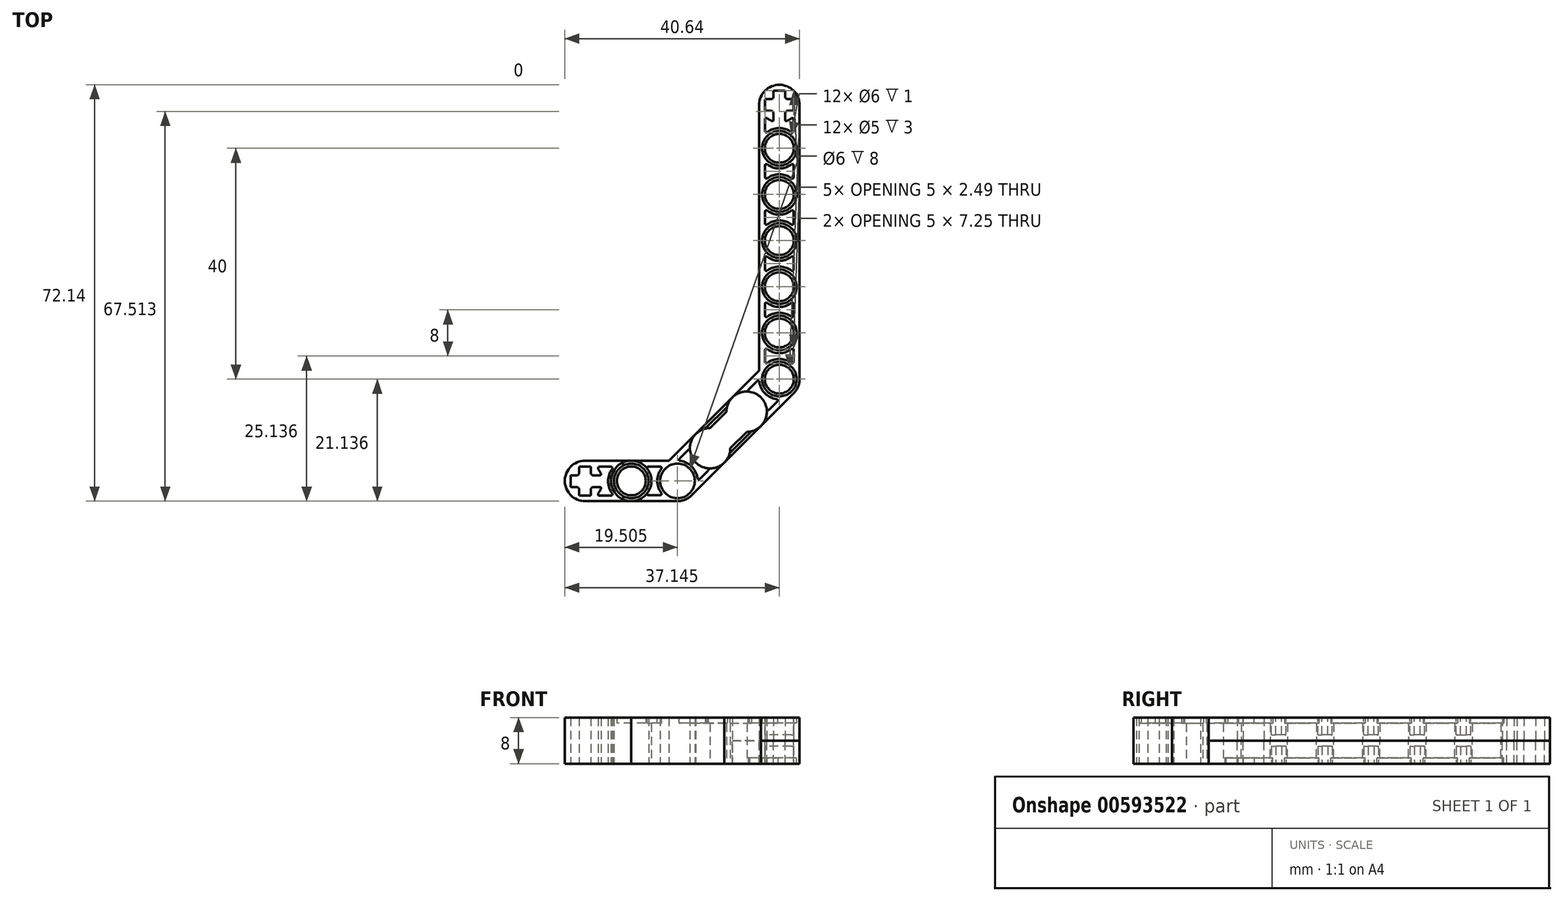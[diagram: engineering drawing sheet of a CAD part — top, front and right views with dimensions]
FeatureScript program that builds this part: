
annotation { "Feature Type Name" : "Feature", "Feature Type Description" : "" }
export const myFeature = defineFeature(function(context is Context, id is Id, definition is map)
    precondition{}
    {
        {
            var Q0;
            Q0=qCreatedBy(makeId("Top.planeOp"),FACE);
            var sketch = newSketch(context, id + "F0", { "sketchPlane" : qUnion([Q0])});
            skArc(sketch, "E0", {"start": v(42.78, 53.86) * mm, "mid": v(39.28, 57.36) * mm, "end": v(35.78, 53.86) * mm});
            skCircle(sketch, "E1", {"center": v(39.28, 6.36) * mm, "radius": 3.5 * mm});
            skLineSegment(sketch, "E2", {"start": v(35.78, 53.86) * mm, "end": v(35.78, 6.36) * mm});
            skLineSegment(sketch, "E3", {"start": v(42.78, 53.86) * mm, "end": v(42.78, 6.36) * mm});
            skCircle(sketch, "E4", {"center": v(39.28, 6.36) * mm, "radius": 2.5 * mm});
            skCircle(sketch, "E5", {"center": v(39.28, 6.36) * mm, "radius": 3 * mm});
            skCircle(sketch, "E6", {"center": v(21.64, -11.28) * mm, "radius": 3.5 * mm});
            skLineSegment(sketch, "E7", {"start": v(21.64, -11.28) * mm, "end": v(5.64, -11.28) * mm});
            skArc(sketch, "E8", {"start": v(5.64, -7.78) * mm, "mid": v(2.14, -11.28) * mm, "end": v(5.64, -14.78) * mm});
            skLineSegment(sketch, "E9", {"start": v(21.64, -7.78) * mm, "end": v(5.64, -7.78) * mm});
            skLineSegment(sketch, "E10", {"start": v(21.64, -14.78) * mm, "end": v(5.64, -14.78) * mm});
            skLineSegment(sketch, "E11", {"start": v(41.76, 3.88) * mm, "end": v(24.12, -13.76) * mm});
            skLineSegment(sketch, "E12", {"start": v(39.28, 6.36) * mm, "end": v(39.28, 14.36) * mm});
            skLineSegment(sketch, "E13", {"start": v(39.28, 14.36) * mm, "end": v(39.28, 22.36) * mm});
            skLineSegment(sketch, "E14", {"start": v(39.28, 22.36) * mm, "end": v(39.28, 30.36) * mm});
            skLineSegment(sketch, "E15", {"start": v(39.28, 30.36) * mm, "end": v(39.28, 38.36) * mm});
            skLineSegment(sketch, "E16", {"start": v(39.28, 38.36) * mm, "end": v(39.28, 46.36) * mm});
            skCircle(sketch, "E17", {"center": v(39.28, 14.36) * mm, "radius": 2.5 * mm});
            skCircle(sketch, "E18", {"center": v(39.28, 14.36) * mm, "radius": 3 * mm});
            skCircle(sketch, "E19", {"center": v(39.28, 14.36) * mm, "radius": 3.5 * mm});
            skCircle(sketch, "E20", {"center": v(39.28, 22.36) * mm, "radius": 2.5 * mm});
            skCircle(sketch, "E21", {"center": v(39.28, 22.36) * mm, "radius": 3 * mm});
            skCircle(sketch, "E22", {"center": v(39.28, 22.36) * mm, "radius": 3.5 * mm});
            skCircle(sketch, "E23", {"center": v(39.28, 30.36) * mm, "radius": 2.5 * mm});
            skCircle(sketch, "E24", {"center": v(39.28, 30.36) * mm, "radius": 3 * mm});
            skCircle(sketch, "E25", {"center": v(39.28, 30.36) * mm, "radius": 3.5 * mm});
            skCircle(sketch, "E26", {"center": v(39.28, 38.36) * mm, "radius": 2.5 * mm});
            skCircle(sketch, "E27", {"center": v(39.28, 38.36) * mm, "radius": 3 * mm});
            skCircle(sketch, "E28", {"center": v(39.28, 38.36) * mm, "radius": 3.5 * mm});
            skCircle(sketch, "E29", {"center": v(39.28, 46.36) * mm, "radius": 2.5 * mm});
            skCircle(sketch, "E30", {"center": v(39.28, 46.36) * mm, "radius": 3 * mm});
            skArc(sketch, "E31", {"start": v(35.78, 46.36) * mm, "mid": v(39.28, 42.86) * mm, "end": v(42.78, 46.36) * mm});
            skLineSegment(sketch, "E32", {"start": v(39.28, 56.36) * mm, "end": v(38.4, 56.36) * mm});
            skLineSegment(sketch, "E33", {"start": v(39.28, 56.36) * mm, "end": v(40.16, 56.36) * mm});
            skLineSegment(sketch, "E34", {"start": v(41.78, 53.86) * mm, "end": v(41.78, 54.74) * mm});
            skLineSegment(sketch, "E35", {"start": v(41.78, 53.86) * mm, "end": v(41.78, 52.98) * mm});
            skLineSegment(sketch, "E36", {"start": v(36.78, 53.86) * mm, "end": v(36.78, 54.74) * mm});
            skLineSegment(sketch, "E37", {"start": v(36.78, 53.86) * mm, "end": v(36.78, 52.98) * mm});
            skLineSegment(sketch, "E38", {"start": v(36.9, 54.86) * mm, "end": v(37.78, 54.86) * mm});
            skLineSegment(sketch, "E39", {"start": v(38.28, 55.36) * mm, "end": v(38.28, 56.24) * mm});
            skLineSegment(sketch, "E40", {"start": v(40.28, 56.24) * mm, "end": v(40.28, 55.36) * mm});
            skLineSegment(sketch, "E41", {"start": v(40.78, 54.86) * mm, "end": v(41.66, 54.86) * mm});
            skLineSegment(sketch, "E42", {"start": v(41.66, 52.86) * mm, "end": v(40.78, 52.86) * mm});
            skLineSegment(sketch, "E43", {"start": v(36.9, 52.86) * mm, "end": v(37.78, 52.86) * mm});
            skPoint(sketch, "E44.visualSharp", {"position": v(38.28, 56.36) * mm});
            skArc(sketch, "E44.filletArc", {"start": v(38.4, 56.36) * mm, "mid": v(38.32, 56.32) * mm, "end": v(38.28, 56.24) * mm});
            skPoint(sketch, "E45.visualSharp", {"position": v(40.28, 56.36) * mm});
            skArc(sketch, "E45.filletArc", {"start": v(40.28, 56.24) * mm, "mid": v(40.25, 56.32) * mm, "end": v(40.16, 56.36) * mm});
            skPoint(sketch, "E46.visualSharp", {"position": v(36.78, 54.86) * mm});
            skArc(sketch, "E46.filletArc", {"start": v(36.9, 54.86) * mm, "mid": v(36.82, 54.82) * mm, "end": v(36.78, 54.74) * mm});
            skPoint(sketch, "E47.visualSharp", {"position": v(36.78, 52.86) * mm});
            skArc(sketch, "E47.filletArc", {"start": v(36.78, 52.98) * mm, "mid": v(36.82, 52.9) * mm, "end": v(36.9, 52.86) * mm});
            skPoint(sketch, "E48.visualSharp", {"position": v(41.78, 54.86) * mm});
            skArc(sketch, "E48.filletArc", {"start": v(41.78, 54.74) * mm, "mid": v(41.75, 54.82) * mm, "end": v(41.66, 54.86) * mm});
            skPoint(sketch, "E49.visualSharp", {"position": v(41.78, 52.86) * mm});
            skArc(sketch, "E49.filletArc", {"start": v(41.66, 52.86) * mm, "mid": v(41.75, 52.9) * mm, "end": v(41.78, 52.98) * mm});
            skPoint(sketch, "E50.visualSharp", {"position": v(38.28, 54.86) * mm});
            skArc(sketch, "E50.filletArc", {"start": v(37.78, 54.86) * mm, "mid": v(38.14, 55) * mm, "end": v(38.28, 55.36) * mm});
            skPoint(sketch, "E51.visualSharp", {"position": v(40.28, 54.86) * mm});
            skArc(sketch, "E51.filletArc", {"start": v(40.28, 55.36) * mm, "mid": v(40.43, 55) * mm, "end": v(40.78, 54.86) * mm});
            skLineSegment(sketch, "E52", {"start": v(36.78, 50.1) * mm, "end": v(36.78, 49.36) * mm});
            skLineSegment(sketch, "E53", {"start": v(36.78, 50.1) * mm, "end": v(36.78, 51.35) * mm});
            skLineSegment(sketch, "E54", {"start": v(41.78, 50.04) * mm, "end": v(41.78, 49.36) * mm});
            skLineSegment(sketch, "E55", {"start": v(41.78, 50.04) * mm, "end": v(41.78, 51.35) * mm});
            skArc(sketch, "E56", {"start": v(37.19, 51.55) * mm, "mid": v(37.59, 51.3) * mm, "end": v(38.01, 51.1) * mm});
            skLineSegment(sketch, "E57.trimOffspring", {"start": v(39.28, 49.36) * mm, "end": v(39.28, 6.36) * mm});
            skLineSegment(sketch, "E58", {"start": v(40.28, 52.36) * mm, "end": v(40.28, 51.28) * mm});
            skLineSegment(sketch, "E59", {"start": v(38.28, 52.36) * mm, "end": v(38.28, 51.28) * mm});
            skPoint(sketch, "E60.visualSharp", {"position": v(38.28, 52.86) * mm});
            skArc(sketch, "E60.filletArc", {"start": v(38.28, 52.36) * mm, "mid": v(38.14, 52.7) * mm, "end": v(37.78, 52.86) * mm});
            skPoint(sketch, "E61.visualSharp", {"position": v(40.28, 52.86) * mm});
            skArc(sketch, "E61.filletArc", {"start": v(40.78, 52.86) * mm, "mid": v(40.43, 52.7) * mm, "end": v(40.28, 52.36) * mm});
            skArc(sketch, "E62.trimOffspring", {"start": v(40.56, 51.1) * mm, "mid": v(40.98, 51.3) * mm, "end": v(41.38, 51.55) * mm});
            skPoint(sketch, "E63.visualSharp", {"position": v(40.28, 51) * mm});
            skArc(sketch, "E63.filletArc", {"start": v(40.28, 51.28) * mm, "mid": v(40.37, 51.12) * mm, "end": v(40.56, 51.1) * mm});
            skPoint(sketch, "E64.visualSharp", {"position": v(38.28, 51) * mm});
            skArc(sketch, "E64.filletArc", {"start": v(38.01, 51.1) * mm, "mid": v(38.2, 51.12) * mm, "end": v(38.28, 51.28) * mm});
            skPoint(sketch, "E65.visualSharp", {"position": v(36.78, 51.9) * mm});
            skArc(sketch, "E65.filletArc", {"start": v(37.19, 51.55) * mm, "mid": v(36.92, 51.58) * mm, "end": v(36.78, 51.35) * mm});
            skArc(sketch, "E66.trimOffspring", {"start": v(41.38, 49.16) * mm, "mid": v(39.28, 49.86) * mm, "end": v(37.19, 49.16) * mm});
            skPoint(sketch, "E67.visualSharp", {"position": v(36.78, 48.8) * mm});
            skArc(sketch, "E67.filletArc", {"start": v(36.78, 49.36) * mm, "mid": v(36.92, 49.14) * mm, "end": v(37.19, 49.16) * mm});
            skPoint(sketch, "E68.visualSharp", {"position": v(41.78, 48.8) * mm});
            skArc(sketch, "E68.filletArc", {"start": v(41.38, 49.16) * mm, "mid": v(41.64, 49.14) * mm, "end": v(41.78, 49.36) * mm});
            skPoint(sketch, "E69.visualSharp", {"position": v(41.78, 51.9) * mm});
            skArc(sketch, "E69.filletArc", {"start": v(41.78, 51.35) * mm, "mid": v(41.64, 51.58) * mm, "end": v(41.38, 51.55) * mm});
            skLineSegment(sketch, "E70", {"start": v(3.13, -11.33) * mm, "end": v(3.13, -12.21) * mm});
            skLineSegment(sketch, "E71", {"start": v(3.13, -11.33) * mm, "end": v(3.13, -10.45) * mm});
            skLineSegment(sketch, "E72", {"start": v(5.63, -8.83) * mm, "end": v(4.75, -8.83) * mm});
            skLineSegment(sketch, "E73", {"start": v(5.63, -8.83) * mm, "end": v(6.51, -8.83) * mm});
            skLineSegment(sketch, "E74", {"start": v(5.63, -13.83) * mm, "end": v(4.75, -13.83) * mm});
            skLineSegment(sketch, "E75", {"start": v(5.63, -13.83) * mm, "end": v(6.51, -13.83) * mm});
            skLineSegment(sketch, "E76", {"start": v(4.63, -13.71) * mm, "end": v(4.63, -12.83) * mm});
            skLineSegment(sketch, "E77", {"start": v(4.13, -12.33) * mm, "end": v(3.25, -12.33) * mm});
            skLineSegment(sketch, "E78", {"start": v(3.25, -10.33) * mm, "end": v(4.13, -10.33) * mm});
            skLineSegment(sketch, "E79", {"start": v(4.63, -9.83) * mm, "end": v(4.63, -8.95) * mm});
            skLineSegment(sketch, "E80", {"start": v(6.63, -8.95) * mm, "end": v(6.63, -9.83) * mm});
            skLineSegment(sketch, "E81", {"start": v(6.63, -13.71) * mm, "end": v(6.63, -12.83) * mm});
            skPoint(sketch, "E82.visualSharp", {"position": v(3.13, -12.33) * mm});
            skArc(sketch, "E82.filletArc", {"start": v(3.13, -12.21) * mm, "mid": v(3.17, -12.3) * mm, "end": v(3.25, -12.33) * mm});
            skPoint(sketch, "E83.visualSharp", {"position": v(3.13, -10.33) * mm});
            skArc(sketch, "E83.filletArc", {"start": v(3.25, -10.33) * mm, "mid": v(3.17, -10.37) * mm, "end": v(3.13, -10.45) * mm});
            skPoint(sketch, "E84.visualSharp", {"position": v(4.63, -13.83) * mm});
            skArc(sketch, "E84.filletArc", {"start": v(4.63, -13.71) * mm, "mid": v(4.67, -13.8) * mm, "end": v(4.75, -13.83) * mm});
            skPoint(sketch, "E85.visualSharp", {"position": v(6.63, -13.83) * mm});
            skArc(sketch, "E85.filletArc", {"start": v(6.51, -13.83) * mm, "mid": v(6.6, -13.8) * mm, "end": v(6.63, -13.71) * mm});
            skPoint(sketch, "E86.visualSharp", {"position": v(4.63, -8.83) * mm});
            skArc(sketch, "E86.filletArc", {"start": v(4.75, -8.83) * mm, "mid": v(4.67, -8.87) * mm, "end": v(4.63, -8.95) * mm});
            skPoint(sketch, "E87.visualSharp", {"position": v(6.63, -8.83) * mm});
            skArc(sketch, "E87.filletArc", {"start": v(6.63, -8.95) * mm, "mid": v(6.6, -8.87) * mm, "end": v(6.51, -8.83) * mm});
            skPoint(sketch, "E88.visualSharp", {"position": v(4.63, -12.33) * mm});
            skArc(sketch, "E88.filletArc", {"start": v(4.63, -12.83) * mm, "mid": v(4.48, -12.48) * mm, "end": v(4.13, -12.33) * mm});
            skPoint(sketch, "E89.visualSharp", {"position": v(4.63, -10.33) * mm});
            skArc(sketch, "E89.filletArc", {"start": v(4.13, -10.33) * mm, "mid": v(4.48, -10.19) * mm, "end": v(4.63, -9.83) * mm});
            skLineSegment(sketch, "E90", {"start": v(9.39, -13.83) * mm, "end": v(10.13, -13.83) * mm});
            skLineSegment(sketch, "E91", {"start": v(9.39, -13.83) * mm, "end": v(8.14, -13.83) * mm});
            skLineSegment(sketch, "E92", {"start": v(9.45, -8.83) * mm, "end": v(10.13, -8.83) * mm});
            skLineSegment(sketch, "E93", {"start": v(9.45, -8.83) * mm, "end": v(8.14, -8.83) * mm});
            skArc(sketch, "E94", {"start": v(7.93, -13.43) * mm, "mid": v(8.2, -13.03) * mm, "end": v(8.4, -12.6) * mm});
            skLineSegment(sketch, "E95", {"start": v(7.13, -10.33) * mm, "end": v(8.2, -10.33) * mm});
            skLineSegment(sketch, "E96", {"start": v(7.13, -12.33) * mm, "end": v(8.2, -12.33) * mm});
            skPoint(sketch, "E97.visualSharp", {"position": v(6.63, -12.33) * mm});
            skArc(sketch, "E97.filletArc", {"start": v(7.13, -12.33) * mm, "mid": v(6.78, -12.48) * mm, "end": v(6.63, -12.83) * mm});
            skPoint(sketch, "E98.visualSharp", {"position": v(6.63, -10.33) * mm});
            skArc(sketch, "E98.filletArc", {"start": v(6.63, -9.83) * mm, "mid": v(6.78, -10.19) * mm, "end": v(7.13, -10.33) * mm});
            skArc(sketch, "E99.trimOffspring", {"start": v(8.4, -10.06) * mm, "mid": v(8.2, -9.63) * mm, "end": v(7.93, -9.24) * mm});
            skPoint(sketch, "E100.visualSharp", {"position": v(8.49, -10.33) * mm});
            skArc(sketch, "E100.filletArc", {"start": v(8.2, -10.33) * mm, "mid": v(8.37, -10.25) * mm, "end": v(8.4, -10.06) * mm});
            skPoint(sketch, "E101.visualSharp", {"position": v(8.49, -12.33) * mm});
            skArc(sketch, "E101.filletArc", {"start": v(8.4, -12.6) * mm, "mid": v(8.37, -12.42) * mm, "end": v(8.2, -12.33) * mm});
            skPoint(sketch, "E102.visualSharp", {"position": v(7.58, -13.83) * mm});
            skArc(sketch, "E102.filletArc", {"start": v(7.93, -13.43) * mm, "mid": v(7.91, -13.7) * mm, "end": v(8.14, -13.83) * mm});
            skArc(sketch, "E103.trimOffspring", {"start": v(10.33, -9.24) * mm, "mid": v(9.63, -11.33) * mm, "end": v(10.33, -13.43) * mm});
            skPoint(sketch, "E104.visualSharp", {"position": v(10.68, -13.83) * mm});
            skArc(sketch, "E104.filletArc", {"start": v(10.13, -13.83) * mm, "mid": v(10.35, -13.7) * mm, "end": v(10.33, -13.43) * mm});
            skPoint(sketch, "E105.visualSharp", {"position": v(10.68, -8.83) * mm});
            skArc(sketch, "E105.filletArc", {"start": v(10.33, -9.24) * mm, "mid": v(10.35, -8.97) * mm, "end": v(10.13, -8.83) * mm});
            skPoint(sketch, "E106.visualSharp", {"position": v(7.58, -8.83) * mm});
            skArc(sketch, "E106.filletArc", {"start": v(8.14, -8.83) * mm, "mid": v(7.91, -8.97) * mm, "end": v(7.93, -9.24) * mm});
            skLineSegment(sketch, "E107", {"start": v(21.64, -11.28) * mm, "end": v(39.28, 6.36) * mm});
            skLineSegment(sketch, "E108", {"start": v(21.64, -11.28) * mm, "end": v(13.64, -11.28) * mm});
            skCircle(sketch, "E109", {"center": v(13.64, -11.28) * mm, "radius": 3.5 * mm});
            skCircle(sketch, "E110", {"center": v(13.64, -11.28) * mm, "radius": 3 * mm});
            skCircle(sketch, "E111", {"center": v(13.64, -11.28) * mm, "radius": 2.5 * mm});
            skCircle(sketch, "E112", {"center": v(21.64, -11.28) * mm, "radius": 3 * mm});
            skCircle(sketch, "E113", {"center": v(21.64, -11.28) * mm, "radius": 2.5 * mm});
            skLineSegment(sketch, "E114", {"start": v(21.64, -11.28) * mm, "end": v(27.3, -5.63) * mm});
            skCircle(sketch, "E115", {"center": v(27.3, -5.63) * mm, "radius": 3.5 * mm});
            skLineSegment(sketch, "E116", {"start": v(39.28, 6.36) * mm, "end": v(33.63, 0.7) * mm});
            skCircle(sketch, "E117", {"center": v(33.63, 0.7) * mm, "radius": 3.5 * mm});
            skLineSegment(sketch, "E118", {"start": v(24.83, -3.15) * mm, "end": v(35.78, 7.8) * mm});
            skLineSegment(sketch, "E119", {"start": v(24.83, -3.15) * mm, "end": v(20.2, -7.78) * mm});
            skCircle(sketch, "E120", {"center": v(27.3, -5.63) * mm, "radius": 3 * mm});
            skCircle(sketch, "E121", {"center": v(27.3, -5.63) * mm, "radius": 2.5 * mm});
            skCircle(sketch, "E122", {"center": v(33.63, 0.7) * mm, "radius": 2.5 * mm});
            skLineSegment(sketch, "E123", {"start": v(31.86, 2.47) * mm, "end": v(25.53, -3.86) * mm});
            skLineSegment(sketch, "E124", {"start": v(29.07, -7.4) * mm, "end": v(35.4, -1.07) * mm});
            skSolve(sketch);
        }
        {
            var Q0;
            Q0=makeQuery(id+"F0.imprint","IMPRINT",FACE,{"disambiguationData":[TD([[makeQuery(id+"F0.imprint","IMPRINT",EDGE,{"derivedFrom":sQuery(id+"F0.wireOp",EDGE,"E70")}),-1.0]])]});
            var Q1;
            {var subQ0=sQuery(id+"F0.wireOp",EDGE,"E92");Q1=makeQuery(id+"F0.imprint","IMPRINT",FACE,{"disambiguationData":[TD([[makeQuery(id+"F0.imprint","IMPRINT",EDGE,{"derivedFrom":subQ0}),1.0]])]});}
            var Q2;
            Q2=makeQuery(id+"F0.imprint","IMPRINT",FACE,{"disambiguationData":[TD([[makeQuery(id+"F0.imprint","IMPRINT",EDGE,{"derivedFrom":sQuery(id+"F0.wireOp",EDGE,"E90")}),-1.0]])]});
            var Q3;
            {var subQ0=sQuery(id+"F0.wireOp",EDGE,"E10");var subQ1=sQuery(id+"F0.wireOp",EDGE,"E6");var subQ2=makeQuery(id+"F0.imprint","INTERSECT",VERTEX,{"derivedFrom":[subQ1,subQ0]});Q3=makeQuery(id+"F0.imprint","IMPRINT",FACE,{"disambiguationData":[TD([[makeQuery(id+"F0.imprint","IMPRINT",EDGE,{"disambiguationData":[TD([[subQ2,1.0]])],"derivedFrom":subQ1}),-1.0]])]});}
            var Q4;
            {var subQ1=sQuery(id+"F0.wireOp",EDGE,"E6");var subQ5=sQuery(id+"F0.wireOp",EDGE,"E9");var subQ6=makeQuery(id+"F0.imprint","INTERSECT",VERTEX,{"derivedFrom":[subQ1,subQ5]});Q4=makeQuery(id+"F0.imprint","IMPRINT",FACE,{"disambiguationData":[TD([[makeQuery(id+"F0.imprint","IMPRINT",EDGE,{"disambiguationData":[TD([[subQ6,-1.0]])],"derivedFrom":subQ1}),-1.0]])]});}
            var Q5;
            {var subQ2=sQuery(id+"F0.wireOp",EDGE,"E7");var subQ6=sQuery(id+"F0.wireOp",EDGE,"E110");var subQ7=makeQuery(id+"F0.imprint","INTERSECT",VERTEX,{"derivedFrom":[subQ2,subQ6]});Q5=makeQuery(id+"F0.imprint","IMPRINT",FACE,{"disambiguationData":[TD([[makeQuery(id+"F0.imprint","IMPRINT",EDGE,{"disambiguationData":[TD([[subQ7,-1.0]])],"derivedFrom":subQ2}),-1.0]])]});}
            var Q6;
            {var subQ4=sQuery(id+"F0.wireOp",EDGE,"E7");var subQ6=sQuery(id+"F0.wireOp",EDGE,"E110");var subQ8=makeQuery(id+"F0.imprint","INTERSECT",VERTEX,{"derivedFrom":[subQ4,subQ6]});Q6=makeQuery(id+"F0.imprint","IMPRINT",FACE,{"disambiguationData":[TD([[makeQuery(id+"F0.imprint","IMPRINT",EDGE,{"disambiguationData":[TD([[subQ8,-1.0]])],"derivedFrom":subQ4}),1.0]])]});}
            var Q7;
            {var subQ1=sQuery(id+"F0.wireOp",EDGE,"E6");var subQ7=makeQuery(id+"F0.imprint","INTERSECT",VERTEX,{"derivedFrom":[subQ1,sQuery(id+"F0.wireOp",EDGE,"E9")]});Q7=makeQuery(id+"F0.imprint","IMPRINT",FACE,{"disambiguationData":[TD([[makeQuery(id+"F0.imprint","IMPRINT",EDGE,{"disambiguationData":[TD([[subQ7,1.0]])],"derivedFrom":subQ1}),1.0]])]});}
            var Q8;
            {var subQ0=sQuery(id+"F0.wireOp",EDGE,"E119");Q8=makeQuery(id+"F0.imprint","IMPRINT",FACE,{"disambiguationData":[TD([[makeQuery(id+"F0.imprint","IMPRINT",EDGE,{"derivedFrom":subQ0}),1.0]])]});}
            var Q9;
            {var subQ0=sQuery(id+"F0.wireOp",EDGE,"E6");var subQ8=makeQuery(id+"F0.imprint","INTERSECT",VERTEX,{"derivedFrom":[subQ0,sQuery(id+"F0.wireOp",EDGE,"E10")]});Q9=makeQuery(id+"F0.imprint","IMPRINT",FACE,{"disambiguationData":[TD([[makeQuery(id+"F0.imprint","IMPRINT",EDGE,{"disambiguationData":[TD([[subQ8,1.0]])],"derivedFrom":subQ0}),1.0]])]});}
            var Q10;
            {var subQ0=sQuery(id+"F0.wireOp",EDGE,"E11");var subQ1=sQuery(id+"F0.wireOp",EDGE,"E6");var subQ2=makeQuery(id+"F0.imprint","INTERSECT",VERTEX,{"derivedFrom":[subQ1,subQ0]});Q10=makeQuery(id+"F0.imprint","IMPRINT",FACE,{"disambiguationData":[TD([[makeQuery(id+"F0.imprint","IMPRINT",EDGE,{"disambiguationData":[TD([[subQ2,-1.0]])],"derivedFrom":subQ1}),-1.0]])]});}
            var Q11;
            {var subQ0=sQuery(id+"F0.wireOp",EDGE,"E115");var subQ5=sQuery(id+"F0.wireOp",EDGE,"E114");var subQ8=makeQuery(id+"F0.imprint","INTERSECT",VERTEX,{"derivedFrom":[subQ5,subQ0]});Q11=makeQuery(id+"F0.imprint","IMPRINT",FACE,{"disambiguationData":[TD([[makeQuery(id+"F0.imprint","IMPRINT",EDGE,{"disambiguationData":[TD([[subQ8,-1.0]])],"derivedFrom":subQ5}),-1.0]])]});}
            var Q12;
            {var subQ0=sQuery(id+"F0.wireOp",EDGE,"E115");var subQ5=sQuery(id+"F0.wireOp",EDGE,"E114");var subQ8=makeQuery(id+"F0.imprint","INTERSECT",VERTEX,{"derivedFrom":[subQ5,subQ0]});Q12=makeQuery(id+"F0.imprint","IMPRINT",FACE,{"disambiguationData":[TD([[makeQuery(id+"F0.imprint","IMPRINT",EDGE,{"disambiguationData":[TD([[subQ8,-1.0]])],"derivedFrom":subQ5}),1.0]])]});}
            var Q13;
            {var subQ0=sQuery(id+"F0.wireOp",EDGE,"E118");var subQ5=sQuery(id+"F0.wireOp",EDGE,"E117");var subQ6=makeQuery(id+"F0.imprint","INTERSECT",VERTEX,{"derivedFrom":[subQ5,subQ0]});Q13=makeQuery(id+"F0.imprint","IMPRINT",FACE,{"disambiguationData":[TD([[makeQuery(id+"F0.imprint","IMPRINT",EDGE,{"disambiguationData":[TD([[subQ6,-1.0]])],"derivedFrom":subQ5}),-1.0]])]});}
            var Q14;
            {var subQ0=sQuery(id+"F0.wireOp",EDGE,"E120");var subQ1=sQuery(id+"F0.wireOp",EDGE,"E114");var subQ2=makeQuery(id+"F0.imprint","INTERSECT",VERTEX,{"derivedFrom":[subQ1,subQ0]});Q14=makeQuery(id+"F0.imprint","IMPRINT",FACE,{"disambiguationData":[TD([[makeQuery(id+"F0.imprint","IMPRINT",EDGE,{"disambiguationData":[TD([[subQ2,-1.0]])],"derivedFrom":subQ1}),1.0]])]});}
            var Q15;
            {var subQ0=sQuery(id+"F0.wireOp",EDGE,"E120");var subQ1=sQuery(id+"F0.wireOp",EDGE,"E114");var subQ2=makeQuery(id+"F0.imprint","INTERSECT",VERTEX,{"derivedFrom":[subQ1,subQ0]});Q15=makeQuery(id+"F0.imprint","IMPRINT",FACE,{"disambiguationData":[TD([[makeQuery(id+"F0.imprint","IMPRINT",EDGE,{"disambiguationData":[TD([[subQ2,-1.0]])],"derivedFrom":subQ1}),-1.0]])]});}
            var Q16;
            {var subQ0=sQuery(id+"F0.wireOp",EDGE,"E117");var subQ1=sQuery(id+"F0.wireOp",EDGE,"E11");var subQ2=makeQuery(id+"F0.imprint","INTERSECT",VERTEX,{"derivedFrom":[subQ1,subQ0]});Q16=makeQuery(id+"F0.imprint","IMPRINT",FACE,{"disambiguationData":[TD([[makeQuery(id+"F0.imprint","IMPRINT",EDGE,{"disambiguationData":[TD([[subQ2,-1.0]])],"derivedFrom":subQ1}),-1.0]])]});}
            var Q17;
            {var subQ3=sQuery(id+"F0.wireOp",EDGE,"E116");var subQ5=sQuery(id+"F0.wireOp",EDGE,"E117");var subQ6=makeQuery(id+"F0.imprint","INTERSECT",VERTEX,{"derivedFrom":[subQ3,subQ5]});Q17=makeQuery(id+"F0.imprint","IMPRINT",FACE,{"disambiguationData":[TD([[makeQuery(id+"F0.imprint","IMPRINT",EDGE,{"disambiguationData":[TD([[subQ6,-1.0]])],"derivedFrom":subQ3}),1.0]])]});}
            var Q18;
            {var subQ3=sQuery(id+"F0.wireOp",EDGE,"E116");var subQ5=sQuery(id+"F0.wireOp",EDGE,"E117");var subQ8=makeQuery(id+"F0.imprint","INTERSECT",VERTEX,{"derivedFrom":[subQ3,subQ5]});Q18=makeQuery(id+"F0.imprint","IMPRINT",FACE,{"disambiguationData":[TD([[makeQuery(id+"F0.imprint","IMPRINT",EDGE,{"disambiguationData":[TD([[subQ8,-1.0]])],"derivedFrom":subQ3}),-1.0]])]});}
            var Q19;
            {var subQ0=sQuery(id+"F0.wireOp",EDGE,"E11");var subQ1=sQuery(id+"F0.wireOp",EDGE,"E1");var subQ2=makeQuery(id+"F0.imprint","INTERSECT",VERTEX,{"derivedFrom":[subQ1,subQ0]});Q19=makeQuery(id+"F0.imprint","IMPRINT",FACE,{"disambiguationData":[TD([[makeQuery(id+"F0.imprint","IMPRINT",EDGE,{"disambiguationData":[TD([[subQ2,1.0]])],"derivedFrom":subQ1}),-1.0]])]});}
            var Q20;
            {var subQ1=sQuery(id+"F0.wireOp",EDGE,"E1");var subQ5=sQuery(id+"F0.wireOp",EDGE,"E2");var subQ6=makeQuery(id+"F0.imprint","INTERSECT",VERTEX,{"derivedFrom":[subQ1,subQ5]});Q20=makeQuery(id+"F0.imprint","IMPRINT",FACE,{"disambiguationData":[TD([[makeQuery(id+"F0.imprint","IMPRINT",EDGE,{"disambiguationData":[TD([[subQ6,-1.0]])],"derivedFrom":subQ1}),-1.0]])]});}
            var Q21;
            {var subQ5=sQuery(id+"F0.wireOp",EDGE,"E1");var subQ6=makeQuery(id+"F0.imprint","INTERSECT",VERTEX,{"derivedFrom":[subQ5,sQuery(id+"F0.wireOp",EDGE,"E3")]});Q21=makeQuery(id+"F0.imprint","IMPRINT",FACE,{"disambiguationData":[TD([[makeQuery(id+"F0.imprint","IMPRINT",EDGE,{"disambiguationData":[TD([[subQ6,-1.0]])],"derivedFrom":subQ5}),1.0]])]});}
            var Q22;
            {var subQ0=sQuery(id+"F0.wireOp",EDGE,"E3");var subQ1=sQuery(id+"F0.wireOp",EDGE,"E1");var subQ2=makeQuery(id+"F0.imprint","INTERSECT",VERTEX,{"derivedFrom":[subQ1,subQ0]});Q22=makeQuery(id+"F0.imprint","IMPRINT",FACE,{"disambiguationData":[TD([[makeQuery(id+"F0.imprint","IMPRINT",EDGE,{"disambiguationData":[TD([[subQ2,-1.0]])],"derivedFrom":subQ1}),-1.0]])]});}
            var Q23;
            {var subQ0=sQuery(id+"F0.wireOp",EDGE,"E2");var subQ6=sQuery(id+"F0.wireOp",EDGE,"E1");var subQ7=makeQuery(id+"F0.imprint","INTERSECT",VERTEX,{"derivedFrom":[subQ6,subQ0]});Q23=makeQuery(id+"F0.imprint","IMPRINT",FACE,{"disambiguationData":[TD([[makeQuery(id+"F0.imprint","IMPRINT",EDGE,{"disambiguationData":[TD([[subQ7,1.0]])],"derivedFrom":subQ6}),-1.0]])]});}
            var Q24;
            {var subQ5=sQuery(id+"F0.wireOp",EDGE,"E1");var subQ7=makeQuery(id+"F0.imprint","INTERSECT",VERTEX,{"derivedFrom":[subQ5,sQuery(id+"F0.wireOp",EDGE,"E2")]});Q24=makeQuery(id+"F0.imprint","IMPRINT",FACE,{"disambiguationData":[TD([[makeQuery(id+"F0.imprint","IMPRINT",EDGE,{"disambiguationData":[TD([[subQ7,1.0]])],"derivedFrom":subQ5}),1.0]])]});}
            var Q25;
            {var subQ0=sQuery(id+"F0.wireOp",EDGE,"E57.trimOffspring");var subQ1=sQuery(id+"F0.wireOp",EDGE,"E18");var subQ2=makeQuery(id+"F0.imprint","INTERSECT",VERTEX,{"disambiguationData":[OD(0.0)],"derivedFrom":[subQ1,subQ0]});Q25=makeQuery(id+"F0.imprint","IMPRINT",FACE,{"disambiguationData":[TD([[makeQuery(id+"F0.imprint","IMPRINT",EDGE,{"disambiguationData":[TD([[subQ2,1.0]])],"derivedFrom":subQ1}),-1.0]])]});}
            var Q26;
            {var subQ0=sQuery(id+"F0.wireOp",EDGE,"E57.trimOffspring");var subQ1=sQuery(id+"F0.wireOp",EDGE,"E18");var subQ2=makeQuery(id+"F0.imprint","INTERSECT",VERTEX,{"disambiguationData":[OD(0.0)],"derivedFrom":[subQ1,subQ0]});Q26=makeQuery(id+"F0.imprint","IMPRINT",FACE,{"disambiguationData":[TD([[makeQuery(id+"F0.imprint","IMPRINT",EDGE,{"disambiguationData":[TD([[subQ2,-1.0]])],"derivedFrom":subQ1}),-1.0]])]});}
            var Q27;
            {var subQ0=sQuery(id+"F0.wireOp",EDGE,"E22");var subQ1=sQuery(id+"F0.wireOp",EDGE,"E3");var subQ2=makeQuery(id+"F0.imprint","INTERSECT",VERTEX,{"derivedFrom":[subQ1,subQ0]});Q27=makeQuery(id+"F0.imprint","IMPRINT",FACE,{"disambiguationData":[TD([[makeQuery(id+"F0.imprint","IMPRINT",EDGE,{"disambiguationData":[TD([[subQ2,-1.0]])],"derivedFrom":subQ1}),-1.0]])]});}
            var Q28;
            {var subQ0=sQuery(id+"F0.wireOp",EDGE,"E22");var subQ1=sQuery(id+"F0.wireOp",EDGE,"E2");var subQ2=makeQuery(id+"F0.imprint","INTERSECT",VERTEX,{"derivedFrom":[subQ1,subQ0]});Q28=makeQuery(id+"F0.imprint","IMPRINT",FACE,{"disambiguationData":[TD([[makeQuery(id+"F0.imprint","IMPRINT",EDGE,{"disambiguationData":[TD([[subQ2,-1.0]])],"derivedFrom":subQ1}),1.0]])]});}
            var Q29;
            {var subQ0=sQuery(id+"F0.wireOp",EDGE,"E57.trimOffspring");var subQ1=sQuery(id+"F0.wireOp",EDGE,"E21");var subQ2=makeQuery(id+"F0.imprint","INTERSECT",VERTEX,{"disambiguationData":[OD(0.0)],"derivedFrom":[subQ1,subQ0]});Q29=makeQuery(id+"F0.imprint","IMPRINT",FACE,{"disambiguationData":[TD([[makeQuery(id+"F0.imprint","IMPRINT",EDGE,{"disambiguationData":[TD([[subQ2,1.0]])],"derivedFrom":subQ1}),-1.0]])]});}
            var Q30;
            {var subQ0=sQuery(id+"F0.wireOp",EDGE,"E25");var subQ1=sQuery(id+"F0.wireOp",EDGE,"E3");var subQ2=makeQuery(id+"F0.imprint","INTERSECT",VERTEX,{"derivedFrom":[subQ1,subQ0]});Q30=makeQuery(id+"F0.imprint","IMPRINT",FACE,{"disambiguationData":[TD([[makeQuery(id+"F0.imprint","IMPRINT",EDGE,{"disambiguationData":[TD([[subQ2,-1.0]])],"derivedFrom":subQ1}),-1.0]])]});}
            var Q31;
            {var subQ0=sQuery(id+"F0.wireOp",EDGE,"E25");var subQ1=sQuery(id+"F0.wireOp",EDGE,"E2");var subQ2=makeQuery(id+"F0.imprint","INTERSECT",VERTEX,{"derivedFrom":[subQ1,subQ0]});Q31=makeQuery(id+"F0.imprint","IMPRINT",FACE,{"disambiguationData":[TD([[makeQuery(id+"F0.imprint","IMPRINT",EDGE,{"disambiguationData":[TD([[subQ2,-1.0]])],"derivedFrom":subQ1}),1.0]])]});}
            var Q32;
            {var subQ2=sQuery(id+"F0.wireOp",EDGE,"E57.trimOffspring");var subQ4=sQuery(id+"F0.wireOp",EDGE,"E21");var subQ5=makeQuery(id+"F0.imprint","INTERSECT",VERTEX,{"disambiguationData":[OD(0.0)],"derivedFrom":[subQ4,subQ2]});Q32=makeQuery(id+"F0.imprint","IMPRINT",FACE,{"disambiguationData":[TD([[makeQuery(id+"F0.imprint","IMPRINT",EDGE,{"disambiguationData":[TD([[subQ5,-1.0]])],"derivedFrom":subQ4}),-1.0]])]});}
            var Q33;
            {var subQ2=sQuery(id+"F0.wireOp",EDGE,"E57.trimOffspring");var subQ4=sQuery(id+"F0.wireOp",EDGE,"E24");var subQ7=makeQuery(id+"F0.imprint","INTERSECT",VERTEX,{"disambiguationData":[OD(0.0)],"derivedFrom":[subQ4,subQ2]});Q33=makeQuery(id+"F0.imprint","IMPRINT",FACE,{"disambiguationData":[TD([[makeQuery(id+"F0.imprint","IMPRINT",EDGE,{"disambiguationData":[TD([[subQ7,1.0]])],"derivedFrom":subQ4}),-1.0]])]});}
            var Q34;
            {var subQ0=sQuery(id+"F0.wireOp",EDGE,"E28");var subQ1=sQuery(id+"F0.wireOp",EDGE,"E3");var subQ2=makeQuery(id+"F0.imprint","INTERSECT",VERTEX,{"derivedFrom":[subQ1,subQ0]});Q34=makeQuery(id+"F0.imprint","IMPRINT",FACE,{"disambiguationData":[TD([[makeQuery(id+"F0.imprint","IMPRINT",EDGE,{"disambiguationData":[TD([[subQ2,-1.0]])],"derivedFrom":subQ1}),-1.0]])]});}
            var Q35;
            {var subQ0=sQuery(id+"F0.wireOp",EDGE,"E28");var subQ1=sQuery(id+"F0.wireOp",EDGE,"E2");var subQ2=makeQuery(id+"F0.imprint","INTERSECT",VERTEX,{"derivedFrom":[subQ1,subQ0]});Q35=makeQuery(id+"F0.imprint","IMPRINT",FACE,{"disambiguationData":[TD([[makeQuery(id+"F0.imprint","IMPRINT",EDGE,{"disambiguationData":[TD([[subQ2,-1.0]])],"derivedFrom":subQ1}),1.0]])]});}
            var Q36;
            {var subQ0=sQuery(id+"F0.wireOp",EDGE,"E57.trimOffspring");var subQ1=sQuery(id+"F0.wireOp",EDGE,"E24");var subQ2=makeQuery(id+"F0.imprint","INTERSECT",VERTEX,{"disambiguationData":[OD(0.0)],"derivedFrom":[subQ1,subQ0]});Q36=makeQuery(id+"F0.imprint","IMPRINT",FACE,{"disambiguationData":[TD([[makeQuery(id+"F0.imprint","IMPRINT",EDGE,{"disambiguationData":[TD([[subQ2,-1.0]])],"derivedFrom":subQ1}),-1.0]])]});}
            var Q37;
            {var subQ0=sQuery(id+"F0.wireOp",EDGE,"E57.trimOffspring");var subQ1=sQuery(id+"F0.wireOp",EDGE,"E27");var subQ2=makeQuery(id+"F0.imprint","INTERSECT",VERTEX,{"disambiguationData":[OD(0.0)],"derivedFrom":[subQ1,subQ0]});Q37=makeQuery(id+"F0.imprint","IMPRINT",FACE,{"disambiguationData":[TD([[makeQuery(id+"F0.imprint","IMPRINT",EDGE,{"disambiguationData":[TD([[subQ2,-1.0]])],"derivedFrom":subQ1}),-1.0]])]});}
            var Q38;
            {var subQ2=sQuery(id+"F0.wireOp",EDGE,"E57.trimOffspring");var subQ4=sQuery(id+"F0.wireOp",EDGE,"E27");var subQ5=makeQuery(id+"F0.imprint","INTERSECT",VERTEX,{"disambiguationData":[OD(0.0)],"derivedFrom":[subQ4,subQ2]});Q38=makeQuery(id+"F0.imprint","IMPRINT",FACE,{"disambiguationData":[TD([[makeQuery(id+"F0.imprint","IMPRINT",EDGE,{"disambiguationData":[TD([[subQ5,1.0]])],"derivedFrom":subQ4}),-1.0]])]});}
            var Q39;
            {var subQ0=sQuery(id+"F0.wireOp",EDGE,"E31");var subQ1=sQuery(id+"F0.wireOp",EDGE,"E3");var subQ2=makeQuery(id+"F0.imprint","INTERSECT",VERTEX,{"derivedFrom":[subQ1,subQ0]});Q39=makeQuery(id+"F0.imprint","IMPRINT",FACE,{"disambiguationData":[TD([[makeQuery(id+"F0.imprint","IMPRINT",EDGE,{"disambiguationData":[TD([[subQ2,-1.0]])],"derivedFrom":subQ1}),-1.0]])]});}
            var Q40;
            {var subQ0=sQuery(id+"F0.wireOp",EDGE,"E31");var subQ1=sQuery(id+"F0.wireOp",EDGE,"E2");var subQ2=makeQuery(id+"F0.imprint","INTERSECT",VERTEX,{"derivedFrom":[subQ1,subQ0]});Q40=makeQuery(id+"F0.imprint","IMPRINT",FACE,{"disambiguationData":[TD([[makeQuery(id+"F0.imprint","IMPRINT",EDGE,{"disambiguationData":[TD([[subQ2,-1.0]])],"derivedFrom":subQ1}),1.0]])]});}
            var Q41;
            {var subQ0=sQuery(id+"F0.wireOp",EDGE,"E0");Q41=makeQuery(id+"F0.imprint","IMPRINT",FACE,{"disambiguationData":[TD([[makeQuery(id+"F0.imprint","IMPRINT",EDGE,{"derivedFrom":subQ0}),1.0]])]});}
            extrude(context, id + "F1", {"entities" : qUnion([Q0, Q1, Q2, Q3, Q4, Q5, Q6, Q7, Q8, Q9, Q10, Q11, Q12, Q13, Q14, Q15, Q16, Q17, Q18, Q19, Q20, Q21, Q22, Q23, Q24, Q25, Q26, Q27, Q28, Q29, Q30, Q31, Q32, Q33, Q34, Q35, Q36, Q37, Q38, Q39, Q40, Q41]), "depth" : 8 * mm, "offsetDistance" : 25 * mm});
        }
        {
            var Q0;
            Q0=makeQuery(id+"F1.opExtrude","CAP_FACE",FACE,{"disambiguationData":[OSD([sQuery(id+"F0.wireOp",EDGE,"E0"),sQuery(id+"F0.wireOp",EDGE,"E1"),sQuery(id+"F0.wireOp",EDGE,"E2"),sQuery(id+"F0.wireOp",EDGE,"E3"),sQuery(id+"F0.wireOp",EDGE,"E5"),sQuery(id+"F0.wireOp",EDGE,"E6"),sQuery(id+"F0.wireOp",EDGE,"E8"),sQuery(id+"F0.wireOp",EDGE,"E9"),sQuery(id+"F0.wireOp",EDGE,"E10"),sQuery(id+"F0.wireOp",EDGE,"E11"),sQuery(id+"F0.wireOp",EDGE,"E18"),sQuery(id+"F0.wireOp",EDGE,"E21"),sQuery(id+"F0.wireOp",EDGE,"E24"),sQuery(id+"F0.wireOp",EDGE,"E27"),sQuery(id+"F0.wireOp",EDGE,"E30"),sQuery(id+"F0.wireOp",EDGE,"E32"),sQuery(id+"F0.wireOp",EDGE,"E33"),sQuery(id+"F0.wireOp",EDGE,"E34"),sQuery(id+"F0.wireOp",EDGE,"E35"),sQuery(id+"F0.wireOp",EDGE,"E36"),sQuery(id+"F0.wireOp",EDGE,"E37"),sQuery(id+"F0.wireOp",EDGE,"E38"),sQuery(id+"F0.wireOp",EDGE,"E39"),sQuery(id+"F0.wireOp",EDGE,"E40"),sQuery(id+"F0.wireOp",EDGE,"E41"),sQuery(id+"F0.wireOp",EDGE,"E42"),sQuery(id+"F0.wireOp",EDGE,"E43"),sQuery(id+"F0.wireOp",EDGE,"E44.filletArc"),sQuery(id+"F0.wireOp",EDGE,"E45.filletArc"),sQuery(id+"F0.wireOp",EDGE,"E46.filletArc"),sQuery(id+"F0.wireOp",EDGE,"E47.filletArc"),sQuery(id+"F0.wireOp",EDGE,"E48.filletArc"),sQuery(id+"F0.wireOp",EDGE,"E49.filletArc"),sQuery(id+"F0.wireOp",EDGE,"E50.filletArc"),sQuery(id+"F0.wireOp",EDGE,"E51.filletArc"),sQuery(id+"F0.wireOp",EDGE,"E52"),sQuery(id+"F0.wireOp",EDGE,"E53"),sQuery(id+"F0.wireOp",EDGE,"E54"),sQuery(id+"F0.wireOp",EDGE,"E55"),sQuery(id+"F0.wireOp",EDGE,"E56"),sQuery(id+"F0.wireOp",EDGE,"E58"),sQuery(id+"F0.wireOp",EDGE,"E59"),sQuery(id+"F0.wireOp",EDGE,"E60.filletArc"),sQuery(id+"F0.wireOp",EDGE,"E61.filletArc"),sQuery(id+"F0.wireOp",EDGE,"E62.trimOffspring"),sQuery(id+"F0.wireOp",EDGE,"E63.filletArc"),sQuery(id+"F0.wireOp",EDGE,"E64.filletArc"),sQuery(id+"F0.wireOp",EDGE,"E65.filletArc"),sQuery(id+"F0.wireOp",EDGE,"E66.trimOffspring"),sQuery(id+"F0.wireOp",EDGE,"E67.filletArc"),sQuery(id+"F0.wireOp",EDGE,"E68.filletArc"),sQuery(id+"F0.wireOp",EDGE,"E69.filletArc"),sQuery(id+"F0.wireOp",EDGE,"E70"),sQuery(id+"F0.wireOp",EDGE,"E71"),sQuery(id+"F0.wireOp",EDGE,"E72"),sQuery(id+"F0.wireOp",EDGE,"E73"),sQuery(id+"F0.wireOp",EDGE,"E74"),sQuery(id+"F0.wireOp",EDGE,"E75"),sQuery(id+"F0.wireOp",EDGE,"E76"),sQuery(id+"F0.wireOp",EDGE,"E77"),sQuery(id+"F0.wireOp",EDGE,"E78"),sQuery(id+"F0.wireOp",EDGE,"E79"),sQuery(id+"F0.wireOp",EDGE,"E80"),sQuery(id+"F0.wireOp",EDGE,"E81"),sQuery(id+"F0.wireOp",EDGE,"E82.filletArc"),sQuery(id+"F0.wireOp",EDGE,"E83.filletArc"),sQuery(id+"F0.wireOp",EDGE,"E84.filletArc"),sQuery(id+"F0.wireOp",EDGE,"E85.filletArc"),sQuery(id+"F0.wireOp",EDGE,"E86.filletArc"),sQuery(id+"F0.wireOp",EDGE,"E87.filletArc"),sQuery(id+"F0.wireOp",EDGE,"E88.filletArc"),sQuery(id+"F0.wireOp",EDGE,"E89.filletArc"),sQuery(id+"F0.wireOp",EDGE,"E90"),sQuery(id+"F0.wireOp",EDGE,"E91"),sQuery(id+"F0.wireOp",EDGE,"E92"),sQuery(id+"F0.wireOp",EDGE,"E93"),sQuery(id+"F0.wireOp",EDGE,"E94"),sQuery(id+"F0.wireOp",EDGE,"E95"),sQuery(id+"F0.wireOp",EDGE,"E96"),sQuery(id+"F0.wireOp",EDGE,"E97.filletArc"),sQuery(id+"F0.wireOp",EDGE,"E98.filletArc"),sQuery(id+"F0.wireOp",EDGE,"E99.trimOffspring"),sQuery(id+"F0.wireOp",EDGE,"E100.filletArc"),sQuery(id+"F0.wireOp",EDGE,"E101.filletArc"),sQuery(id+"F0.wireOp",EDGE,"E102.filletArc"),sQuery(id+"F0.wireOp",EDGE,"E103.trimOffspring"),sQuery(id+"F0.wireOp",EDGE,"E104.filletArc"),sQuery(id+"F0.wireOp",EDGE,"E105.filletArc"),sQuery(id+"F0.wireOp",EDGE,"E106.filletArc"),sQuery(id+"F0.wireOp",EDGE,"E110"),sQuery(id+"F0.wireOp",EDGE,"E112"),sQuery(id+"F0.wireOp",EDGE,"E118"),sQuery(id+"F0.wireOp",EDGE,"E119"),sQuery(id+"F0.wireOp",EDGE,"E121"),sQuery(id+"F0.wireOp",EDGE,"E122"),sQuery(id+"F0.wireOp",EDGE,"E123"),sQuery(id+"F0.wireOp",EDGE,"E124")])],"isStart":false});
            var sketch = newSketch(context, id + "F2", { "sketchPlane" : qUnion([Q0])});
            skArc(sketch, "E125", {"start": v(37.19, 43.55) * mm, "mid": v(39.28, 42.86) * mm, "end": v(41.38, 43.55) * mm});
            skArc(sketch, "E126", {"start": v(41.38, 41.16) * mm, "mid": v(39.28, 41.86) * mm, "end": v(37.19, 41.16) * mm});
            skLineSegment(sketch, "E127", {"start": v(36.78, 42.33) * mm, "end": v(36.78, 41.36) * mm});
            skLineSegment(sketch, "E128", {"start": v(36.78, 42.33) * mm, "end": v(36.78, 43.35) * mm});
            skLineSegment(sketch, "E129", {"start": v(41.78, 42.42) * mm, "end": v(41.78, 41.36) * mm});
            skLineSegment(sketch, "E130", {"start": v(41.78, 42.42) * mm, "end": v(41.78, 43.35) * mm});
            skPoint(sketch, "E131.visualSharp", {"position": v(36.78, 40.8) * mm});
            skArc(sketch, "E131.filletArc", {"start": v(36.78, 41.36) * mm, "mid": v(36.92, 41.14) * mm, "end": v(37.19, 41.16) * mm});
            skPoint(sketch, "E132.visualSharp", {"position": v(36.78, 43.9) * mm});
            skArc(sketch, "E132.filletArc", {"start": v(37.19, 43.55) * mm, "mid": v(36.92, 43.58) * mm, "end": v(36.78, 43.35) * mm});
            skPoint(sketch, "E133.visualSharp", {"position": v(41.78, 43.9) * mm});
            skArc(sketch, "E133.filletArc", {"start": v(41.78, 43.35) * mm, "mid": v(41.64, 43.58) * mm, "end": v(41.38, 43.55) * mm});
            skPoint(sketch, "E134.visualSharp", {"position": v(41.78, 40.8) * mm});
            skArc(sketch, "E134.filletArc", {"start": v(41.38, 41.16) * mm, "mid": v(41.64, 41.14) * mm, "end": v(41.78, 41.36) * mm});
            skArc(sketch, "E135.0.1.0", {"start": v(41.38, 33.16) * mm, "mid": v(39.28, 33.86) * mm, "end": v(37.19, 33.16) * mm});
            skLineSegment(sketch, "E135.0.1.1", {"start": v(36.78, 34.33) * mm, "end": v(36.78, 33.36) * mm});
            skArc(sketch, "E135.0.1.2", {"start": v(36.78, 33.36) * mm, "mid": v(36.92, 33.14) * mm, "end": v(37.19, 33.16) * mm});
            skLineSegment(sketch, "E135.0.1.3", {"start": v(36.78, 34.33) * mm, "end": v(36.78, 35.35) * mm});
            skArc(sketch, "E135.0.1.4", {"start": v(37.19, 35.55) * mm, "mid": v(36.92, 35.58) * mm, "end": v(36.78, 35.35) * mm});
            skArc(sketch, "E135.0.1.5", {"start": v(37.19, 35.55) * mm, "mid": v(39.28, 34.86) * mm, "end": v(41.38, 35.55) * mm});
            skLineSegment(sketch, "E135.0.1.6", {"start": v(41.78, 34.42) * mm, "end": v(41.78, 33.36) * mm});
            skArc(sketch, "E135.0.1.7", {"start": v(41.38, 33.16) * mm, "mid": v(41.64, 33.14) * mm, "end": v(41.78, 33.36) * mm});
            skLineSegment(sketch, "E135.0.1.8", {"start": v(41.78, 34.42) * mm, "end": v(41.78, 35.35) * mm});
            skArc(sketch, "E135.0.1.9", {"start": v(41.78, 35.35) * mm, "mid": v(41.64, 35.58) * mm, "end": v(41.38, 35.55) * mm});
            skArc(sketch, "E135.0.2.0", {"start": v(41.38, 25.16) * mm, "mid": v(39.28, 25.86) * mm, "end": v(37.19, 25.16) * mm});
            skLineSegment(sketch, "E135.0.2.1", {"start": v(36.78, 26.33) * mm, "end": v(36.78, 25.36) * mm});
            skArc(sketch, "E135.0.2.2", {"start": v(36.78, 25.36) * mm, "mid": v(36.92, 25.14) * mm, "end": v(37.19, 25.16) * mm});
            skLineSegment(sketch, "E135.0.2.3", {"start": v(36.78, 26.33) * mm, "end": v(36.78, 27.35) * mm});
            skArc(sketch, "E135.0.2.4", {"start": v(37.19, 27.55) * mm, "mid": v(36.92, 27.58) * mm, "end": v(36.78, 27.35) * mm});
            skArc(sketch, "E135.0.2.5", {"start": v(37.19, 27.55) * mm, "mid": v(39.28, 26.86) * mm, "end": v(41.38, 27.55) * mm});
            skLineSegment(sketch, "E135.0.2.6", {"start": v(41.78, 26.42) * mm, "end": v(41.78, 25.36) * mm});
            skArc(sketch, "E135.0.2.7", {"start": v(41.38, 25.16) * mm, "mid": v(41.64, 25.14) * mm, "end": v(41.78, 25.36) * mm});
            skLineSegment(sketch, "E135.0.2.8", {"start": v(41.78, 26.42) * mm, "end": v(41.78, 27.35) * mm});
            skArc(sketch, "E135.0.2.9", {"start": v(41.78, 27.35) * mm, "mid": v(41.64, 27.58) * mm, "end": v(41.38, 27.55) * mm});
            skArc(sketch, "E135.0.3.0", {"start": v(41.38, 17.16) * mm, "mid": v(39.28, 17.86) * mm, "end": v(37.19, 17.16) * mm});
            skLineSegment(sketch, "E135.0.3.1", {"start": v(36.78, 18.33) * mm, "end": v(36.78, 17.36) * mm});
            skArc(sketch, "E135.0.3.2", {"start": v(36.78, 17.36) * mm, "mid": v(36.92, 17.14) * mm, "end": v(37.19, 17.16) * mm});
            skLineSegment(sketch, "E135.0.3.3", {"start": v(36.78, 18.33) * mm, "end": v(36.78, 19.35) * mm});
            skArc(sketch, "E135.0.3.4", {"start": v(37.19, 19.55) * mm, "mid": v(36.92, 19.58) * mm, "end": v(36.78, 19.35) * mm});
            skArc(sketch, "E135.0.3.5", {"start": v(37.19, 19.55) * mm, "mid": v(39.28, 18.86) * mm, "end": v(41.38, 19.55) * mm});
            skLineSegment(sketch, "E135.0.3.6", {"start": v(41.78, 18.42) * mm, "end": v(41.78, 17.36) * mm});
            skArc(sketch, "E135.0.3.7", {"start": v(41.38, 17.16) * mm, "mid": v(41.64, 17.14) * mm, "end": v(41.78, 17.36) * mm});
            skLineSegment(sketch, "E135.0.3.8", {"start": v(41.78, 18.42) * mm, "end": v(41.78, 19.35) * mm});
            skArc(sketch, "E135.0.3.9", {"start": v(41.78, 19.35) * mm, "mid": v(41.64, 19.58) * mm, "end": v(41.38, 19.55) * mm});
            skArc(sketch, "E135.0.4.0", {"start": v(41.38, 9.16) * mm, "mid": v(39.28, 9.86) * mm, "end": v(37.19, 9.16) * mm});
            skLineSegment(sketch, "E135.0.4.1", {"start": v(36.78, 10.33) * mm, "end": v(36.78, 9.36) * mm});
            skArc(sketch, "E135.0.4.2", {"start": v(36.78, 9.36) * mm, "mid": v(36.92, 9.14) * mm, "end": v(37.19, 9.16) * mm});
            skLineSegment(sketch, "E135.0.4.3", {"start": v(36.78, 10.33) * mm, "end": v(36.78, 11.35) * mm});
            skArc(sketch, "E135.0.4.4", {"start": v(37.19, 11.55) * mm, "mid": v(36.92, 11.58) * mm, "end": v(36.78, 11.35) * mm});
            skArc(sketch, "E135.0.4.5", {"start": v(37.19, 11.55) * mm, "mid": v(39.28, 10.86) * mm, "end": v(41.38, 11.55) * mm});
            skLineSegment(sketch, "E135.0.4.6", {"start": v(41.78, 10.42) * mm, "end": v(41.78, 9.36) * mm});
            skArc(sketch, "E135.0.4.7", {"start": v(41.38, 9.16) * mm, "mid": v(41.64, 9.14) * mm, "end": v(41.78, 9.36) * mm});
            skLineSegment(sketch, "E135.0.4.8", {"start": v(41.78, 10.42) * mm, "end": v(41.78, 11.35) * mm});
            skArc(sketch, "E135.0.4.9", {"start": v(41.78, 11.35) * mm, "mid": v(41.64, 11.58) * mm, "end": v(41.38, 11.55) * mm});
            skLineSegment(sketch, "E135.direction1", {"start": v(39.28, 38.36) * mm, "end": v(64.28, 38.36) * mm, "construction": true});
            skLineSegment(sketch, "E135.direction2", {"start": v(39.28, 38.36) * mm, "end": v(39.28, 30.36) * mm, "construction": true});
            skSolve(sketch);
        }
        {
            var Q0;
            Q0=qSketchRegion(id+"F2",true);
            extrude(context, id + "F3", {"entities" : qUnion([Q0]), "operationType" : NewBodyOperationType.REMOVE, "oppositeDirection" : true, "depth" : 3 * mm, "offsetDistance" : 25 * mm});
        }
        {
            var Q0;
            {var subQ0=sQuery(id+"F0.wireOp",EDGE,"E57.trimOffspring");var subQ1=sQuery(id+"F0.wireOp",EDGE,"E29");var subQ2=makeQuery(id+"F0.imprint","INTERSECT",VERTEX,{"disambiguationData":[OD(0.0)],"derivedFrom":[subQ1,subQ0]});Q0=makeQuery(id+"F0.imprint","IMPRINT",FACE,{"disambiguationData":[TD([[makeQuery(id+"F0.imprint","IMPRINT",EDGE,{"disambiguationData":[TD([[subQ2,-1.0]])],"derivedFrom":subQ1}),-1.0]])]});}
            var Q1;
            {var subQ0=sQuery(id+"F0.wireOp",EDGE,"E57.trimOffspring");var subQ1=sQuery(id+"F0.wireOp",EDGE,"E29");var subQ2=makeQuery(id+"F0.imprint","INTERSECT",VERTEX,{"disambiguationData":[OD(0.0)],"derivedFrom":[subQ1,subQ0]});Q1=makeQuery(id+"F0.imprint","IMPRINT",FACE,{"disambiguationData":[TD([[makeQuery(id+"F0.imprint","IMPRINT",EDGE,{"disambiguationData":[TD([[subQ2,1.0]])],"derivedFrom":subQ1}),-1.0]])]});}
            var Q2;
            {var subQ0=sQuery(id+"F0.wireOp",EDGE,"E57.trimOffspring");var subQ1=sQuery(id+"F0.wireOp",EDGE,"E26");var subQ2=makeQuery(id+"F0.imprint","INTERSECT",VERTEX,{"disambiguationData":[OD(0.0)],"derivedFrom":[subQ1,subQ0]});Q2=makeQuery(id+"F0.imprint","IMPRINT",FACE,{"disambiguationData":[TD([[makeQuery(id+"F0.imprint","IMPRINT",EDGE,{"disambiguationData":[TD([[subQ2,-1.0]])],"derivedFrom":subQ1}),-1.0]])]});}
            var Q3;
            {var subQ0=sQuery(id+"F0.wireOp",EDGE,"E57.trimOffspring");var subQ1=sQuery(id+"F0.wireOp",EDGE,"E26");var subQ2=makeQuery(id+"F0.imprint","INTERSECT",VERTEX,{"disambiguationData":[OD(0.0)],"derivedFrom":[subQ1,subQ0]});Q3=makeQuery(id+"F0.imprint","IMPRINT",FACE,{"disambiguationData":[TD([[makeQuery(id+"F0.imprint","IMPRINT",EDGE,{"disambiguationData":[TD([[subQ2,1.0]])],"derivedFrom":subQ1}),-1.0]])]});}
            var Q4;
            {var subQ0=sQuery(id+"F0.wireOp",EDGE,"E57.trimOffspring");var subQ1=sQuery(id+"F0.wireOp",EDGE,"E23");var subQ2=makeQuery(id+"F0.imprint","INTERSECT",VERTEX,{"disambiguationData":[OD(0.0)],"derivedFrom":[subQ1,subQ0]});Q4=makeQuery(id+"F0.imprint","IMPRINT",FACE,{"disambiguationData":[TD([[makeQuery(id+"F0.imprint","IMPRINT",EDGE,{"disambiguationData":[TD([[subQ2,-1.0]])],"derivedFrom":subQ1}),-1.0]])]});}
            var Q5;
            {var subQ0=sQuery(id+"F0.wireOp",EDGE,"E57.trimOffspring");var subQ1=sQuery(id+"F0.wireOp",EDGE,"E23");var subQ2=makeQuery(id+"F0.imprint","INTERSECT",VERTEX,{"disambiguationData":[OD(0.0)],"derivedFrom":[subQ1,subQ0]});Q5=makeQuery(id+"F0.imprint","IMPRINT",FACE,{"disambiguationData":[TD([[makeQuery(id+"F0.imprint","IMPRINT",EDGE,{"disambiguationData":[TD([[subQ2,1.0]])],"derivedFrom":subQ1}),-1.0]])]});}
            var Q6;
            {var subQ0=sQuery(id+"F0.wireOp",EDGE,"E57.trimOffspring");var subQ1=sQuery(id+"F0.wireOp",EDGE,"E20");var subQ2=makeQuery(id+"F0.imprint","INTERSECT",VERTEX,{"disambiguationData":[OD(0.0)],"derivedFrom":[subQ1,subQ0]});Q6=makeQuery(id+"F0.imprint","IMPRINT",FACE,{"disambiguationData":[TD([[makeQuery(id+"F0.imprint","IMPRINT",EDGE,{"disambiguationData":[TD([[subQ2,-1.0]])],"derivedFrom":subQ1}),-1.0]])]});}
            var Q7;
            {var subQ0=sQuery(id+"F0.wireOp",EDGE,"E57.trimOffspring");var subQ1=sQuery(id+"F0.wireOp",EDGE,"E20");var subQ2=makeQuery(id+"F0.imprint","INTERSECT",VERTEX,{"disambiguationData":[OD(0.0)],"derivedFrom":[subQ1,subQ0]});Q7=makeQuery(id+"F0.imprint","IMPRINT",FACE,{"disambiguationData":[TD([[makeQuery(id+"F0.imprint","IMPRINT",EDGE,{"disambiguationData":[TD([[subQ2,1.0]])],"derivedFrom":subQ1}),-1.0]])]});}
            var Q8;
            {var subQ0=sQuery(id+"F0.wireOp",EDGE,"E57.trimOffspring");var subQ1=sQuery(id+"F0.wireOp",EDGE,"E17");var subQ2=makeQuery(id+"F0.imprint","INTERSECT",VERTEX,{"disambiguationData":[OD(0.0)],"derivedFrom":[subQ1,subQ0]});Q8=makeQuery(id+"F0.imprint","IMPRINT",FACE,{"disambiguationData":[TD([[makeQuery(id+"F0.imprint","IMPRINT",EDGE,{"disambiguationData":[TD([[subQ2,-1.0]])],"derivedFrom":subQ1}),-1.0]])]});}
            var Q9;
            {var subQ0=sQuery(id+"F0.wireOp",EDGE,"E57.trimOffspring");var subQ1=sQuery(id+"F0.wireOp",EDGE,"E17");var subQ2=makeQuery(id+"F0.imprint","INTERSECT",VERTEX,{"disambiguationData":[OD(0.0)],"derivedFrom":[subQ1,subQ0]});Q9=makeQuery(id+"F0.imprint","IMPRINT",FACE,{"disambiguationData":[TD([[makeQuery(id+"F0.imprint","IMPRINT",EDGE,{"disambiguationData":[TD([[subQ2,1.0]])],"derivedFrom":subQ1}),-1.0]])]});}
            var Q10;
            {var subQ0=sQuery(id+"F0.wireOp",EDGE,"E57.trimOffspring");var subQ1=sQuery(id+"F0.wireOp",EDGE,"E4");var subQ2=makeQuery(id+"F0.imprint","INTERSECT",VERTEX,{"derivedFrom":[subQ1,subQ0]});Q10=makeQuery(id+"F0.imprint","IMPRINT",FACE,{"disambiguationData":[TD([[makeQuery(id+"F0.imprint","IMPRINT",EDGE,{"disambiguationData":[TD([[subQ2,-1.0]])],"derivedFrom":subQ1}),-1.0]])]});}
            var Q11;
            {var subQ0=sQuery(id+"F0.wireOp",EDGE,"E57.trimOffspring");var subQ1=sQuery(id+"F0.wireOp",EDGE,"E4");var subQ2=makeQuery(id+"F0.imprint","INTERSECT",VERTEX,{"derivedFrom":[subQ1,subQ0]});Q11=makeQuery(id+"F0.imprint","IMPRINT",FACE,{"disambiguationData":[TD([[makeQuery(id+"F0.imprint","IMPRINT",EDGE,{"disambiguationData":[TD([[subQ2,1.0]])],"derivedFrom":subQ1}),-1.0]])]});}
            var Q12;
            {var subQ0=sQuery(id+"F0.wireOp",EDGE,"E113");var subQ1=sQuery(id+"F0.wireOp",EDGE,"E108");var subQ2=makeQuery(id+"F0.imprint","INTERSECT",VERTEX,{"derivedFrom":[subQ1,subQ0]});Q12=makeQuery(id+"F0.imprint","IMPRINT",FACE,{"disambiguationData":[TD([[makeQuery(id+"F0.imprint","IMPRINT",EDGE,{"disambiguationData":[TD([[subQ2,-1.0]])],"derivedFrom":subQ1}),-1.0]])]});}
            var Q13;
            {var subQ0=sQuery(id+"F0.wireOp",EDGE,"E113");var subQ1=sQuery(id+"F0.wireOp",EDGE,"E108");var subQ2=makeQuery(id+"F0.imprint","INTERSECT",VERTEX,{"derivedFrom":[subQ1,subQ0]});Q13=makeQuery(id+"F0.imprint","IMPRINT",FACE,{"disambiguationData":[TD([[makeQuery(id+"F0.imprint","IMPRINT",EDGE,{"disambiguationData":[TD([[subQ2,-1.0]])],"derivedFrom":subQ1}),1.0]])]});}
            var Q14;
            {var subQ0=sQuery(id+"F0.wireOp",EDGE,"E111");var subQ1=sQuery(id+"F0.wireOp",EDGE,"E7");var subQ2=makeQuery(id+"F0.imprint","INTERSECT",VERTEX,{"derivedFrom":[subQ1,subQ0]});Q14=makeQuery(id+"F0.imprint","IMPRINT",FACE,{"disambiguationData":[TD([[makeQuery(id+"F0.imprint","IMPRINT",EDGE,{"disambiguationData":[TD([[subQ2,-1.0]])],"derivedFrom":subQ1}),-1.0]])]});}
            var Q15;
            {var subQ0=sQuery(id+"F0.wireOp",EDGE,"E111");var subQ1=sQuery(id+"F0.wireOp",EDGE,"E7");var subQ2=makeQuery(id+"F0.imprint","INTERSECT",VERTEX,{"derivedFrom":[subQ1,subQ0]});Q15=makeQuery(id+"F0.imprint","IMPRINT",FACE,{"disambiguationData":[TD([[makeQuery(id+"F0.imprint","IMPRINT",EDGE,{"disambiguationData":[TD([[subQ2,-1.0]])],"derivedFrom":subQ1}),1.0]])]});}
            extrude(context, id + "F4", {"entities" : qUnion([Q0, Q1, Q2, Q3, Q4, Q5, Q6, Q7, Q8, Q9, Q10, Q11, Q12, Q13, Q14, Q15]), "operationType" : NewBodyOperationType.ADD, "depth" : 7 * mm, "offsetDistance" : 25 * mm});
        }
        {
            var Q0;
            Q0=makeQuery(id+"F1.opExtrude","CAP_FACE",FACE,{"disambiguationData":[OSD([sQuery(id+"F0.wireOp",EDGE,"E0"),sQuery(id+"F0.wireOp",EDGE,"E1"),sQuery(id+"F0.wireOp",EDGE,"E2"),sQuery(id+"F0.wireOp",EDGE,"E3"),sQuery(id+"F0.wireOp",EDGE,"E5"),sQuery(id+"F0.wireOp",EDGE,"E6"),sQuery(id+"F0.wireOp",EDGE,"E8"),sQuery(id+"F0.wireOp",EDGE,"E9"),sQuery(id+"F0.wireOp",EDGE,"E10"),sQuery(id+"F0.wireOp",EDGE,"E11"),sQuery(id+"F0.wireOp",EDGE,"E18"),sQuery(id+"F0.wireOp",EDGE,"E21"),sQuery(id+"F0.wireOp",EDGE,"E24"),sQuery(id+"F0.wireOp",EDGE,"E27"),sQuery(id+"F0.wireOp",EDGE,"E30"),sQuery(id+"F0.wireOp",EDGE,"E32"),sQuery(id+"F0.wireOp",EDGE,"E33"),sQuery(id+"F0.wireOp",EDGE,"E34"),sQuery(id+"F0.wireOp",EDGE,"E35"),sQuery(id+"F0.wireOp",EDGE,"E36"),sQuery(id+"F0.wireOp",EDGE,"E37"),sQuery(id+"F0.wireOp",EDGE,"E38"),sQuery(id+"F0.wireOp",EDGE,"E39"),sQuery(id+"F0.wireOp",EDGE,"E40"),sQuery(id+"F0.wireOp",EDGE,"E41"),sQuery(id+"F0.wireOp",EDGE,"E42"),sQuery(id+"F0.wireOp",EDGE,"E43"),sQuery(id+"F0.wireOp",EDGE,"E44.filletArc"),sQuery(id+"F0.wireOp",EDGE,"E45.filletArc"),sQuery(id+"F0.wireOp",EDGE,"E46.filletArc"),sQuery(id+"F0.wireOp",EDGE,"E47.filletArc"),sQuery(id+"F0.wireOp",EDGE,"E48.filletArc"),sQuery(id+"F0.wireOp",EDGE,"E49.filletArc"),sQuery(id+"F0.wireOp",EDGE,"E50.filletArc"),sQuery(id+"F0.wireOp",EDGE,"E51.filletArc"),sQuery(id+"F0.wireOp",EDGE,"E52"),sQuery(id+"F0.wireOp",EDGE,"E53"),sQuery(id+"F0.wireOp",EDGE,"E54"),sQuery(id+"F0.wireOp",EDGE,"E55"),sQuery(id+"F0.wireOp",EDGE,"E56"),sQuery(id+"F0.wireOp",EDGE,"E58"),sQuery(id+"F0.wireOp",EDGE,"E59"),sQuery(id+"F0.wireOp",EDGE,"E60.filletArc"),sQuery(id+"F0.wireOp",EDGE,"E61.filletArc"),sQuery(id+"F0.wireOp",EDGE,"E62.trimOffspring"),sQuery(id+"F0.wireOp",EDGE,"E63.filletArc"),sQuery(id+"F0.wireOp",EDGE,"E64.filletArc"),sQuery(id+"F0.wireOp",EDGE,"E65.filletArc"),sQuery(id+"F0.wireOp",EDGE,"E66.trimOffspring"),sQuery(id+"F0.wireOp",EDGE,"E67.filletArc"),sQuery(id+"F0.wireOp",EDGE,"E68.filletArc"),sQuery(id+"F0.wireOp",EDGE,"E69.filletArc"),sQuery(id+"F0.wireOp",EDGE,"E70"),sQuery(id+"F0.wireOp",EDGE,"E71"),sQuery(id+"F0.wireOp",EDGE,"E72"),sQuery(id+"F0.wireOp",EDGE,"E73"),sQuery(id+"F0.wireOp",EDGE,"E74"),sQuery(id+"F0.wireOp",EDGE,"E75"),sQuery(id+"F0.wireOp",EDGE,"E76"),sQuery(id+"F0.wireOp",EDGE,"E77"),sQuery(id+"F0.wireOp",EDGE,"E78"),sQuery(id+"F0.wireOp",EDGE,"E79"),sQuery(id+"F0.wireOp",EDGE,"E80"),sQuery(id+"F0.wireOp",EDGE,"E81"),sQuery(id+"F0.wireOp",EDGE,"E82.filletArc"),sQuery(id+"F0.wireOp",EDGE,"E83.filletArc"),sQuery(id+"F0.wireOp",EDGE,"E84.filletArc"),sQuery(id+"F0.wireOp",EDGE,"E85.filletArc"),sQuery(id+"F0.wireOp",EDGE,"E86.filletArc"),sQuery(id+"F0.wireOp",EDGE,"E87.filletArc"),sQuery(id+"F0.wireOp",EDGE,"E88.filletArc"),sQuery(id+"F0.wireOp",EDGE,"E89.filletArc"),sQuery(id+"F0.wireOp",EDGE,"E90"),sQuery(id+"F0.wireOp",EDGE,"E91"),sQuery(id+"F0.wireOp",EDGE,"E92"),sQuery(id+"F0.wireOp",EDGE,"E93"),sQuery(id+"F0.wireOp",EDGE,"E94"),sQuery(id+"F0.wireOp",EDGE,"E95"),sQuery(id+"F0.wireOp",EDGE,"E96"),sQuery(id+"F0.wireOp",EDGE,"E97.filletArc"),sQuery(id+"F0.wireOp",EDGE,"E98.filletArc"),sQuery(id+"F0.wireOp",EDGE,"E99.trimOffspring"),sQuery(id+"F0.wireOp",EDGE,"E100.filletArc"),sQuery(id+"F0.wireOp",EDGE,"E101.filletArc"),sQuery(id+"F0.wireOp",EDGE,"E102.filletArc"),sQuery(id+"F0.wireOp",EDGE,"E103.trimOffspring"),sQuery(id+"F0.wireOp",EDGE,"E104.filletArc"),sQuery(id+"F0.wireOp",EDGE,"E105.filletArc"),sQuery(id+"F0.wireOp",EDGE,"E106.filletArc"),sQuery(id+"F0.wireOp",EDGE,"E110"),sQuery(id+"F0.wireOp",EDGE,"E112"),sQuery(id+"F0.wireOp",EDGE,"E118"),sQuery(id+"F0.wireOp",EDGE,"E119"),sQuery(id+"F0.wireOp",EDGE,"E121"),sQuery(id+"F0.wireOp",EDGE,"E122"),sQuery(id+"F0.wireOp",EDGE,"E123"),sQuery(id+"F0.wireOp",EDGE,"E124")])],"isStart":false});
            var sketch = newSketch(context, id + "F5", { "sketchPlane" : qUnion([Q0])});
            skArc(sketch, "E136", {"start": v(25.18, -3.5) * mm, "mid": v(25.18, -7.75) * mm, "end": v(29.42, -7.75) * mm});
            skArc(sketch, "E137", {"start": v(35.75, -1.42) * mm, "mid": v(35.75, 2.82) * mm, "end": v(31.5, 2.82) * mm});
            skLineSegment(sketch, "E138", {"start": v(25.18, -3.5) * mm, "end": v(31.5, 2.82) * mm});
            skLineSegment(sketch, "E139", {"start": v(29.42, -7.75) * mm, "end": v(35.78, -1.39) * mm});
            skSolve(sketch);
        }
        {
            var Q0;
            {var subQ1=sQuery(id+"F5.wireOp",EDGE,"E136");Q0=makeQuery(id+"F5.imprint","IMPRINT",FACE,{"disambiguationData":[TD([[makeQuery(id+"F5.imprint","IMPRINT",EDGE,{"derivedFrom":subQ1}),1.0]])]});}
            extrude(context, id + "F6", {"entities" : qUnion([Q0]), "operationType" : NewBodyOperationType.REMOVE, "oppositeDirection" : true, "depth" : 1 * mm, "offsetDistance" : 25 * mm});
        }
        {
            var Q0;
            Q0=makeQuery(id+"F1.opExtrude","CAP_FACE",FACE,{"disambiguationData":[OSD([sQuery(id+"F0.wireOp",EDGE,"E0"),sQuery(id+"F0.wireOp",EDGE,"E1"),sQuery(id+"F0.wireOp",EDGE,"E2"),sQuery(id+"F0.wireOp",EDGE,"E3"),sQuery(id+"F0.wireOp",EDGE,"E5"),sQuery(id+"F0.wireOp",EDGE,"E6"),sQuery(id+"F0.wireOp",EDGE,"E8"),sQuery(id+"F0.wireOp",EDGE,"E9"),sQuery(id+"F0.wireOp",EDGE,"E10"),sQuery(id+"F0.wireOp",EDGE,"E11"),sQuery(id+"F0.wireOp",EDGE,"E18"),sQuery(id+"F0.wireOp",EDGE,"E21"),sQuery(id+"F0.wireOp",EDGE,"E24"),sQuery(id+"F0.wireOp",EDGE,"E27"),sQuery(id+"F0.wireOp",EDGE,"E30"),sQuery(id+"F0.wireOp",EDGE,"E32"),sQuery(id+"F0.wireOp",EDGE,"E33"),sQuery(id+"F0.wireOp",EDGE,"E34"),sQuery(id+"F0.wireOp",EDGE,"E35"),sQuery(id+"F0.wireOp",EDGE,"E36"),sQuery(id+"F0.wireOp",EDGE,"E37"),sQuery(id+"F0.wireOp",EDGE,"E38"),sQuery(id+"F0.wireOp",EDGE,"E39"),sQuery(id+"F0.wireOp",EDGE,"E40"),sQuery(id+"F0.wireOp",EDGE,"E41"),sQuery(id+"F0.wireOp",EDGE,"E42"),sQuery(id+"F0.wireOp",EDGE,"E43"),sQuery(id+"F0.wireOp",EDGE,"E44.filletArc"),sQuery(id+"F0.wireOp",EDGE,"E45.filletArc"),sQuery(id+"F0.wireOp",EDGE,"E46.filletArc"),sQuery(id+"F0.wireOp",EDGE,"E47.filletArc"),sQuery(id+"F0.wireOp",EDGE,"E48.filletArc"),sQuery(id+"F0.wireOp",EDGE,"E49.filletArc"),sQuery(id+"F0.wireOp",EDGE,"E50.filletArc"),sQuery(id+"F0.wireOp",EDGE,"E51.filletArc"),sQuery(id+"F0.wireOp",EDGE,"E52"),sQuery(id+"F0.wireOp",EDGE,"E53"),sQuery(id+"F0.wireOp",EDGE,"E54"),sQuery(id+"F0.wireOp",EDGE,"E55"),sQuery(id+"F0.wireOp",EDGE,"E56"),sQuery(id+"F0.wireOp",EDGE,"E58"),sQuery(id+"F0.wireOp",EDGE,"E59"),sQuery(id+"F0.wireOp",EDGE,"E60.filletArc"),sQuery(id+"F0.wireOp",EDGE,"E61.filletArc"),sQuery(id+"F0.wireOp",EDGE,"E62.trimOffspring"),sQuery(id+"F0.wireOp",EDGE,"E63.filletArc"),sQuery(id+"F0.wireOp",EDGE,"E64.filletArc"),sQuery(id+"F0.wireOp",EDGE,"E65.filletArc"),sQuery(id+"F0.wireOp",EDGE,"E66.trimOffspring"),sQuery(id+"F0.wireOp",EDGE,"E67.filletArc"),sQuery(id+"F0.wireOp",EDGE,"E68.filletArc"),sQuery(id+"F0.wireOp",EDGE,"E69.filletArc"),sQuery(id+"F0.wireOp",EDGE,"E70"),sQuery(id+"F0.wireOp",EDGE,"E71"),sQuery(id+"F0.wireOp",EDGE,"E72"),sQuery(id+"F0.wireOp",EDGE,"E73"),sQuery(id+"F0.wireOp",EDGE,"E74"),sQuery(id+"F0.wireOp",EDGE,"E75"),sQuery(id+"F0.wireOp",EDGE,"E76"),sQuery(id+"F0.wireOp",EDGE,"E77"),sQuery(id+"F0.wireOp",EDGE,"E78"),sQuery(id+"F0.wireOp",EDGE,"E79"),sQuery(id+"F0.wireOp",EDGE,"E80"),sQuery(id+"F0.wireOp",EDGE,"E81"),sQuery(id+"F0.wireOp",EDGE,"E82.filletArc"),sQuery(id+"F0.wireOp",EDGE,"E83.filletArc"),sQuery(id+"F0.wireOp",EDGE,"E84.filletArc"),sQuery(id+"F0.wireOp",EDGE,"E85.filletArc"),sQuery(id+"F0.wireOp",EDGE,"E86.filletArc"),sQuery(id+"F0.wireOp",EDGE,"E87.filletArc"),sQuery(id+"F0.wireOp",EDGE,"E88.filletArc"),sQuery(id+"F0.wireOp",EDGE,"E89.filletArc"),sQuery(id+"F0.wireOp",EDGE,"E90"),sQuery(id+"F0.wireOp",EDGE,"E91"),sQuery(id+"F0.wireOp",EDGE,"E92"),sQuery(id+"F0.wireOp",EDGE,"E93"),sQuery(id+"F0.wireOp",EDGE,"E94"),sQuery(id+"F0.wireOp",EDGE,"E95"),sQuery(id+"F0.wireOp",EDGE,"E96"),sQuery(id+"F0.wireOp",EDGE,"E97.filletArc"),sQuery(id+"F0.wireOp",EDGE,"E98.filletArc"),sQuery(id+"F0.wireOp",EDGE,"E99.trimOffspring"),sQuery(id+"F0.wireOp",EDGE,"E100.filletArc"),sQuery(id+"F0.wireOp",EDGE,"E101.filletArc"),sQuery(id+"F0.wireOp",EDGE,"E102.filletArc"),sQuery(id+"F0.wireOp",EDGE,"E103.trimOffspring"),sQuery(id+"F0.wireOp",EDGE,"E104.filletArc"),sQuery(id+"F0.wireOp",EDGE,"E105.filletArc"),sQuery(id+"F0.wireOp",EDGE,"E106.filletArc"),sQuery(id+"F0.wireOp",EDGE,"E110"),sQuery(id+"F0.wireOp",EDGE,"E112"),sQuery(id+"F0.wireOp",EDGE,"E118"),sQuery(id+"F0.wireOp",EDGE,"E119"),sQuery(id+"F0.wireOp",EDGE,"E121"),sQuery(id+"F0.wireOp",EDGE,"E122"),sQuery(id+"F0.wireOp",EDGE,"E123"),sQuery(id+"F0.wireOp",EDGE,"E124")])],"isStart":false});
            var sketch = newSketch(context, id + "F7", { "sketchPlane" : qUnion([Q0])});
            skArc(sketch, "E140", {"start": v(35.82, 5.86) * mm, "mid": v(36.8, 3.88) * mm, "end": v(38.78, 2.9) * mm});
            skArc(sketch, "E141", {"start": v(37.1, 1.2) * mm, "mid": v(36.1, 3.17) * mm, "end": v(34.13, 4.16) * mm});
            skArc(sketch, "E142", {"start": v(23.84, -6.13) * mm, "mid": v(24.83, -8.1) * mm, "end": v(26.8, -9.1) * mm});
            skArc(sketch, "E143", {"start": v(25.1, -10.78) * mm, "mid": v(24.12, -8.8) * mm, "end": v(22.15, -7.82) * mm});
            skLineSegment(sketch, "E144", {"start": v(38.08, 1.61) * mm, "end": v(37.52, 1.06) * mm});
            skLineSegment(sketch, "E145", {"start": v(38.08, 1.61) * mm, "end": v(38.93, 2.46) * mm});
            skLineSegment(sketch, "E146", {"start": v(26.1, -10.36) * mm, "end": v(26.94, -9.52) * mm});
            skLineSegment(sketch, "E147", {"start": v(26.1, -10.36) * mm, "end": v(25.54, -10.93) * mm});
            skLineSegment(sketch, "E148", {"start": v(23.4, -5.98) * mm, "end": v(22, -7.4) * mm});
            skLineSegment(sketch, "E149", {"start": v(35.4, 6) * mm, "end": v(33.99, 4.6) * mm});
            skPoint(sketch, "E150.visualSharp", {"position": v(33.6, 4.2) * mm});
            skArc(sketch, "E150.filletArc", {"start": v(33.99, 4.6) * mm, "mid": v(33.92, 4.33) * mm, "end": v(34.13, 4.16) * mm});
            skPoint(sketch, "E151.visualSharp", {"position": v(35.78, 6.4) * mm});
            skArc(sketch, "E151.filletArc", {"start": v(35.82, 5.86) * mm, "mid": v(35.65, 6.06) * mm, "end": v(35.4, 6) * mm});
            skPoint(sketch, "E152.visualSharp", {"position": v(37.13, 0.66) * mm});
            skArc(sketch, "E152.filletArc", {"start": v(37.1, 1.2) * mm, "mid": v(37.26, 1) * mm, "end": v(37.52, 1.06) * mm});
            skPoint(sketch, "E153.visualSharp", {"position": v(39.32, 2.86) * mm});
            skArc(sketch, "E153.filletArc", {"start": v(38.93, 2.46) * mm, "mid": v(38.99, 2.72) * mm, "end": v(38.78, 2.9) * mm});
            skPoint(sketch, "E154.visualSharp", {"position": v(21.6, -7.78) * mm});
            skArc(sketch, "E154.filletArc", {"start": v(22, -7.4) * mm, "mid": v(21.94, -7.65) * mm, "end": v(22.15, -7.82) * mm});
            skPoint(sketch, "E155.visualSharp", {"position": v(23.8, -5.6) * mm});
            skArc(sketch, "E155.filletArc", {"start": v(23.84, -6.13) * mm, "mid": v(23.67, -5.92) * mm, "end": v(23.4, -5.98) * mm});
            skPoint(sketch, "E156.visualSharp", {"position": v(25.14, -11.32) * mm});
            skArc(sketch, "E156.filletArc", {"start": v(25.1, -10.78) * mm, "mid": v(25.28, -10.99) * mm, "end": v(25.54, -10.93) * mm});
            skPoint(sketch, "E157.visualSharp", {"position": v(27.34, -9.13) * mm});
            skArc(sketch, "E157.filletArc", {"start": v(26.94, -9.52) * mm, "mid": v(27, -9.26) * mm, "end": v(26.8, -9.1) * mm});
            skSolve(sketch);
        }
        {
            var Q0;
            Q0=qSketchRegion(id+"F7",true);
            extrude(context, id + "F8", {"entities" : qUnion([Q0]), "operationType" : NewBodyOperationType.REMOVE, "oppositeDirection" : true, "depth" : 1 * mm, "offsetDistance" : 25 * mm});
        }
        {
            var Q0;
            Q0=makeQuery(id+"F1.opExtrude","CAP_FACE",FACE,{"disambiguationData":[OSD([sQuery(id+"F0.wireOp",EDGE,"E0"),sQuery(id+"F0.wireOp",EDGE,"E1"),sQuery(id+"F0.wireOp",EDGE,"E2"),sQuery(id+"F0.wireOp",EDGE,"E3"),sQuery(id+"F0.wireOp",EDGE,"E5"),sQuery(id+"F0.wireOp",EDGE,"E6"),sQuery(id+"F0.wireOp",EDGE,"E8"),sQuery(id+"F0.wireOp",EDGE,"E9"),sQuery(id+"F0.wireOp",EDGE,"E10"),sQuery(id+"F0.wireOp",EDGE,"E11"),sQuery(id+"F0.wireOp",EDGE,"E18"),sQuery(id+"F0.wireOp",EDGE,"E21"),sQuery(id+"F0.wireOp",EDGE,"E24"),sQuery(id+"F0.wireOp",EDGE,"E27"),sQuery(id+"F0.wireOp",EDGE,"E30"),sQuery(id+"F0.wireOp",EDGE,"E32"),sQuery(id+"F0.wireOp",EDGE,"E33"),sQuery(id+"F0.wireOp",EDGE,"E34"),sQuery(id+"F0.wireOp",EDGE,"E35"),sQuery(id+"F0.wireOp",EDGE,"E36"),sQuery(id+"F0.wireOp",EDGE,"E37"),sQuery(id+"F0.wireOp",EDGE,"E38"),sQuery(id+"F0.wireOp",EDGE,"E39"),sQuery(id+"F0.wireOp",EDGE,"E40"),sQuery(id+"F0.wireOp",EDGE,"E41"),sQuery(id+"F0.wireOp",EDGE,"E42"),sQuery(id+"F0.wireOp",EDGE,"E43"),sQuery(id+"F0.wireOp",EDGE,"E44.filletArc"),sQuery(id+"F0.wireOp",EDGE,"E45.filletArc"),sQuery(id+"F0.wireOp",EDGE,"E46.filletArc"),sQuery(id+"F0.wireOp",EDGE,"E47.filletArc"),sQuery(id+"F0.wireOp",EDGE,"E48.filletArc"),sQuery(id+"F0.wireOp",EDGE,"E49.filletArc"),sQuery(id+"F0.wireOp",EDGE,"E50.filletArc"),sQuery(id+"F0.wireOp",EDGE,"E51.filletArc"),sQuery(id+"F0.wireOp",EDGE,"E52"),sQuery(id+"F0.wireOp",EDGE,"E53"),sQuery(id+"F0.wireOp",EDGE,"E54"),sQuery(id+"F0.wireOp",EDGE,"E55"),sQuery(id+"F0.wireOp",EDGE,"E56"),sQuery(id+"F0.wireOp",EDGE,"E58"),sQuery(id+"F0.wireOp",EDGE,"E59"),sQuery(id+"F0.wireOp",EDGE,"E60.filletArc"),sQuery(id+"F0.wireOp",EDGE,"E61.filletArc"),sQuery(id+"F0.wireOp",EDGE,"E62.trimOffspring"),sQuery(id+"F0.wireOp",EDGE,"E63.filletArc"),sQuery(id+"F0.wireOp",EDGE,"E64.filletArc"),sQuery(id+"F0.wireOp",EDGE,"E65.filletArc"),sQuery(id+"F0.wireOp",EDGE,"E66.trimOffspring"),sQuery(id+"F0.wireOp",EDGE,"E67.filletArc"),sQuery(id+"F0.wireOp",EDGE,"E68.filletArc"),sQuery(id+"F0.wireOp",EDGE,"E69.filletArc"),sQuery(id+"F0.wireOp",EDGE,"E70"),sQuery(id+"F0.wireOp",EDGE,"E71"),sQuery(id+"F0.wireOp",EDGE,"E72"),sQuery(id+"F0.wireOp",EDGE,"E73"),sQuery(id+"F0.wireOp",EDGE,"E74"),sQuery(id+"F0.wireOp",EDGE,"E75"),sQuery(id+"F0.wireOp",EDGE,"E76"),sQuery(id+"F0.wireOp",EDGE,"E77"),sQuery(id+"F0.wireOp",EDGE,"E78"),sQuery(id+"F0.wireOp",EDGE,"E79"),sQuery(id+"F0.wireOp",EDGE,"E80"),sQuery(id+"F0.wireOp",EDGE,"E81"),sQuery(id+"F0.wireOp",EDGE,"E82.filletArc"),sQuery(id+"F0.wireOp",EDGE,"E83.filletArc"),sQuery(id+"F0.wireOp",EDGE,"E84.filletArc"),sQuery(id+"F0.wireOp",EDGE,"E85.filletArc"),sQuery(id+"F0.wireOp",EDGE,"E86.filletArc"),sQuery(id+"F0.wireOp",EDGE,"E87.filletArc"),sQuery(id+"F0.wireOp",EDGE,"E88.filletArc"),sQuery(id+"F0.wireOp",EDGE,"E89.filletArc"),sQuery(id+"F0.wireOp",EDGE,"E90"),sQuery(id+"F0.wireOp",EDGE,"E91"),sQuery(id+"F0.wireOp",EDGE,"E92"),sQuery(id+"F0.wireOp",EDGE,"E93"),sQuery(id+"F0.wireOp",EDGE,"E94"),sQuery(id+"F0.wireOp",EDGE,"E95"),sQuery(id+"F0.wireOp",EDGE,"E96"),sQuery(id+"F0.wireOp",EDGE,"E97.filletArc"),sQuery(id+"F0.wireOp",EDGE,"E98.filletArc"),sQuery(id+"F0.wireOp",EDGE,"E99.trimOffspring"),sQuery(id+"F0.wireOp",EDGE,"E100.filletArc"),sQuery(id+"F0.wireOp",EDGE,"E101.filletArc"),sQuery(id+"F0.wireOp",EDGE,"E102.filletArc"),sQuery(id+"F0.wireOp",EDGE,"E103.trimOffspring"),sQuery(id+"F0.wireOp",EDGE,"E104.filletArc"),sQuery(id+"F0.wireOp",EDGE,"E105.filletArc"),sQuery(id+"F0.wireOp",EDGE,"E106.filletArc"),sQuery(id+"F0.wireOp",EDGE,"E110"),sQuery(id+"F0.wireOp",EDGE,"E112"),sQuery(id+"F0.wireOp",EDGE,"E118"),sQuery(id+"F0.wireOp",EDGE,"E119"),sQuery(id+"F0.wireOp",EDGE,"E121"),sQuery(id+"F0.wireOp",EDGE,"E122"),sQuery(id+"F0.wireOp",EDGE,"E123"),sQuery(id+"F0.wireOp",EDGE,"E124")])],"isStart":false});
            var sketch = newSketch(context, id + "F9", { "sketchPlane" : qUnion([Q0])});
            skArc(sketch, "E158", {"start": v(18.84, -9.19) * mm, "mid": v(18.14, -11.28) * mm, "end": v(18.84, -13.38) * mm});
            skArc(sketch, "E159", {"start": v(16.45, -13.38) * mm, "mid": v(17.14, -11.28) * mm, "end": v(16.45, -9.19) * mm});
            skLineSegment(sketch, "E160", {"start": v(17.62, -13.78) * mm, "end": v(16.65, -13.78) * mm});
            skLineSegment(sketch, "E161", {"start": v(17.62, -13.78) * mm, "end": v(18.64, -13.78) * mm});
            skLineSegment(sketch, "E162", {"start": v(18.64, -8.78) * mm, "end": v(16.65, -8.78) * mm});
            skPoint(sketch, "E163.visualSharp", {"position": v(16.1, -8.78) * mm});
            skArc(sketch, "E163.filletArc", {"start": v(16.65, -8.78) * mm, "mid": v(16.42, -8.92) * mm, "end": v(16.45, -9.19) * mm});
            skPoint(sketch, "E164.visualSharp", {"position": v(19.2, -8.78) * mm});
            skArc(sketch, "E164.filletArc", {"start": v(18.84, -9.19) * mm, "mid": v(18.86, -8.92) * mm, "end": v(18.64, -8.78) * mm});
            skPoint(sketch, "E165.visualSharp", {"position": v(19.2, -13.78) * mm});
            skArc(sketch, "E165.filletArc", {"start": v(18.64, -13.78) * mm, "mid": v(18.86, -13.64) * mm, "end": v(18.84, -13.38) * mm});
            skPoint(sketch, "E166.visualSharp", {"position": v(16.1, -13.78) * mm});
            skArc(sketch, "E166.filletArc", {"start": v(16.45, -13.38) * mm, "mid": v(16.42, -13.64) * mm, "end": v(16.65, -13.78) * mm});
            skSolve(sketch);
        }
        {
            var Q0;
            Q0=qSketchRegion(id+"F9",true);
            extrude(context, id + "F10", {"entities" : qUnion([Q0]), "operationType" : NewBodyOperationType.REMOVE, "oppositeDirection" : true, "depth" : 1 * mm, "offsetDistance" : 25 * mm});
        }
        {
            var Q0;
            {var subQ0=sQuery(id+"F0.wireOp",EDGE,"E112");var subQ1=sQuery(id+"F0.wireOp",EDGE,"E110");var subQ2=sQuery(id+"F0.wireOp",EDGE,"E30");var subQ3=sQuery(id+"F0.wireOp",EDGE,"E27");var subQ4=sQuery(id+"F0.wireOp",EDGE,"E24");var subQ5=sQuery(id+"F0.wireOp",EDGE,"E21");var subQ6=sQuery(id+"F0.wireOp",EDGE,"E18");var subQ7=sQuery(id+"F0.wireOp",EDGE,"E5");Q0=makeQuery(id+"F4.boolean.opBoolean","MERGE",FACE,{"derivedFrom":[makeQuery(id+"F1.opExtrude","CAP_FACE",FACE,{"disambiguationData":[OSD([sQuery(id+"F0.wireOp",EDGE,"E0"),sQuery(id+"F0.wireOp",EDGE,"E1"),sQuery(id+"F0.wireOp",EDGE,"E2"),sQuery(id+"F0.wireOp",EDGE,"E3"),subQ7,sQuery(id+"F0.wireOp",EDGE,"E6"),sQuery(id+"F0.wireOp",EDGE,"E8"),sQuery(id+"F0.wireOp",EDGE,"E9"),sQuery(id+"F0.wireOp",EDGE,"E10"),sQuery(id+"F0.wireOp",EDGE,"E11"),subQ6,subQ5,subQ4,subQ3,subQ2,sQuery(id+"F0.wireOp",EDGE,"E32"),sQuery(id+"F0.wireOp",EDGE,"E33"),sQuery(id+"F0.wireOp",EDGE,"E34"),sQuery(id+"F0.wireOp",EDGE,"E35"),sQuery(id+"F0.wireOp",EDGE,"E36"),sQuery(id+"F0.wireOp",EDGE,"E37"),sQuery(id+"F0.wireOp",EDGE,"E38"),sQuery(id+"F0.wireOp",EDGE,"E39"),sQuery(id+"F0.wireOp",EDGE,"E40"),sQuery(id+"F0.wireOp",EDGE,"E41"),sQuery(id+"F0.wireOp",EDGE,"E42"),sQuery(id+"F0.wireOp",EDGE,"E43"),sQuery(id+"F0.wireOp",EDGE,"E44.filletArc"),sQuery(id+"F0.wireOp",EDGE,"E45.filletArc"),sQuery(id+"F0.wireOp",EDGE,"E46.filletArc"),sQuery(id+"F0.wireOp",EDGE,"E47.filletArc"),sQuery(id+"F0.wireOp",EDGE,"E48.filletArc"),sQuery(id+"F0.wireOp",EDGE,"E49.filletArc"),sQuery(id+"F0.wireOp",EDGE,"E50.filletArc"),sQuery(id+"F0.wireOp",EDGE,"E51.filletArc"),sQuery(id+"F0.wireOp",EDGE,"E52"),sQuery(id+"F0.wireOp",EDGE,"E53"),sQuery(id+"F0.wireOp",EDGE,"E54"),sQuery(id+"F0.wireOp",EDGE,"E55"),sQuery(id+"F0.wireOp",EDGE,"E56"),sQuery(id+"F0.wireOp",EDGE,"E58"),sQuery(id+"F0.wireOp",EDGE,"E59"),sQuery(id+"F0.wireOp",EDGE,"E60.filletArc"),sQuery(id+"F0.wireOp",EDGE,"E61.filletArc"),sQuery(id+"F0.wireOp",EDGE,"E62.trimOffspring"),sQuery(id+"F0.wireOp",EDGE,"E63.filletArc"),sQuery(id+"F0.wireOp",EDGE,"E64.filletArc"),sQuery(id+"F0.wireOp",EDGE,"E65.filletArc"),sQuery(id+"F0.wireOp",EDGE,"E66.trimOffspring"),sQuery(id+"F0.wireOp",EDGE,"E67.filletArc"),sQuery(id+"F0.wireOp",EDGE,"E68.filletArc"),sQuery(id+"F0.wireOp",EDGE,"E69.filletArc"),sQuery(id+"F0.wireOp",EDGE,"E70"),sQuery(id+"F0.wireOp",EDGE,"E71"),sQuery(id+"F0.wireOp",EDGE,"E72"),sQuery(id+"F0.wireOp",EDGE,"E73"),sQuery(id+"F0.wireOp",EDGE,"E74"),sQuery(id+"F0.wireOp",EDGE,"E75"),sQuery(id+"F0.wireOp",EDGE,"E76"),sQuery(id+"F0.wireOp",EDGE,"E77"),sQuery(id+"F0.wireOp",EDGE,"E78"),sQuery(id+"F0.wireOp",EDGE,"E79"),sQuery(id+"F0.wireOp",EDGE,"E80"),sQuery(id+"F0.wireOp",EDGE,"E81"),sQuery(id+"F0.wireOp",EDGE,"E82.filletArc"),sQuery(id+"F0.wireOp",EDGE,"E83.filletArc"),sQuery(id+"F0.wireOp",EDGE,"E84.filletArc"),sQuery(id+"F0.wireOp",EDGE,"E85.filletArc"),sQuery(id+"F0.wireOp",EDGE,"E86.filletArc"),sQuery(id+"F0.wireOp",EDGE,"E87.filletArc"),sQuery(id+"F0.wireOp",EDGE,"E88.filletArc"),sQuery(id+"F0.wireOp",EDGE,"E89.filletArc"),sQuery(id+"F0.wireOp",EDGE,"E90"),sQuery(id+"F0.wireOp",EDGE,"E91"),sQuery(id+"F0.wireOp",EDGE,"E92"),sQuery(id+"F0.wireOp",EDGE,"E93"),sQuery(id+"F0.wireOp",EDGE,"E94"),sQuery(id+"F0.wireOp",EDGE,"E95"),sQuery(id+"F0.wireOp",EDGE,"E96"),sQuery(id+"F0.wireOp",EDGE,"E97.filletArc"),sQuery(id+"F0.wireOp",EDGE,"E98.filletArc"),sQuery(id+"F0.wireOp",EDGE,"E99.trimOffspring"),sQuery(id+"F0.wireOp",EDGE,"E100.filletArc"),sQuery(id+"F0.wireOp",EDGE,"E101.filletArc"),sQuery(id+"F0.wireOp",EDGE,"E102.filletArc"),sQuery(id+"F0.wireOp",EDGE,"E103.trimOffspring"),sQuery(id+"F0.wireOp",EDGE,"E104.filletArc"),sQuery(id+"F0.wireOp",EDGE,"E105.filletArc"),sQuery(id+"F0.wireOp",EDGE,"E106.filletArc"),subQ1,subQ0,sQuery(id+"F0.wireOp",EDGE,"E118"),sQuery(id+"F0.wireOp",EDGE,"E119"),sQuery(id+"F0.wireOp",EDGE,"E121"),sQuery(id+"F0.wireOp",EDGE,"E122"),sQuery(id+"F0.wireOp",EDGE,"E123"),sQuery(id+"F0.wireOp",EDGE,"E124")])],"isStart":true}),makeQuery(id+"F4.opExtrude","CAP_FACE",FACE,{"disambiguationData":[OSD([sQuery(id+"F0.wireOp",EDGE,"E4"),subQ7])],"isStart":true}),makeQuery(id+"F4.opExtrude","CAP_FACE",FACE,{"disambiguationData":[OSD([sQuery(id+"F0.wireOp",EDGE,"E17"),subQ6])],"isStart":true}),makeQuery(id+"F4.opExtrude","CAP_FACE",FACE,{"disambiguationData":[OSD([sQuery(id+"F0.wireOp",EDGE,"E20"),subQ5])],"isStart":true}),makeQuery(id+"F4.opExtrude","CAP_FACE",FACE,{"disambiguationData":[OSD([sQuery(id+"F0.wireOp",EDGE,"E23"),subQ4])],"isStart":true}),makeQuery(id+"F4.opExtrude","CAP_FACE",FACE,{"disambiguationData":[OSD([sQuery(id+"F0.wireOp",EDGE,"E26"),subQ3])],"isStart":true}),makeQuery(id+"F4.opExtrude","CAP_FACE",FACE,{"disambiguationData":[OSD([sQuery(id+"F0.wireOp",EDGE,"E29"),subQ2])],"isStart":true}),makeQuery(id+"F4.opExtrude","CAP_FACE",FACE,{"disambiguationData":[OSD([subQ1,sQuery(id+"F0.wireOp",EDGE,"E111")])],"isStart":true}),makeQuery(id+"F4.opExtrude","CAP_FACE",FACE,{"disambiguationData":[OSD([subQ0,sQuery(id+"F0.wireOp",EDGE,"E113")])],"isStart":true})]});}
            extrude(context, id + "F11", {"entities" : qUnion([Q0]), "operationType" : NewBodyOperationType.REMOVE, "oppositeDirection" : true, "depth" : 4 * mm, "offsetDistance" : 25 * mm});
        }
        {
            var Q0;
            Q0=makeQuery(id+"F1.opExtrude","SWEPT_BODY",BODY,{"disambiguationData":[OSD([sQuery(id+"F0.wireOp",EDGE,"E0"),sQuery(id+"F0.wireOp",EDGE,"E1"),sQuery(id+"F0.wireOp",EDGE,"E2"),sQuery(id+"F0.wireOp",EDGE,"E3"),sQuery(id+"F0.wireOp",EDGE,"E5"),sQuery(id+"F0.wireOp",EDGE,"E6"),sQuery(id+"F0.wireOp",EDGE,"E8"),sQuery(id+"F0.wireOp",EDGE,"E9"),sQuery(id+"F0.wireOp",EDGE,"E10"),sQuery(id+"F0.wireOp",EDGE,"E11"),sQuery(id+"F0.wireOp",EDGE,"E18"),sQuery(id+"F0.wireOp",EDGE,"E21"),sQuery(id+"F0.wireOp",EDGE,"E24"),sQuery(id+"F0.wireOp",EDGE,"E27"),sQuery(id+"F0.wireOp",EDGE,"E30"),sQuery(id+"F0.wireOp",EDGE,"E32"),sQuery(id+"F0.wireOp",EDGE,"E33"),sQuery(id+"F0.wireOp",EDGE,"E34"),sQuery(id+"F0.wireOp",EDGE,"E35"),sQuery(id+"F0.wireOp",EDGE,"E36"),sQuery(id+"F0.wireOp",EDGE,"E37"),sQuery(id+"F0.wireOp",EDGE,"E38"),sQuery(id+"F0.wireOp",EDGE,"E39"),sQuery(id+"F0.wireOp",EDGE,"E40"),sQuery(id+"F0.wireOp",EDGE,"E41"),sQuery(id+"F0.wireOp",EDGE,"E42"),sQuery(id+"F0.wireOp",EDGE,"E43"),sQuery(id+"F0.wireOp",EDGE,"E44.filletArc"),sQuery(id+"F0.wireOp",EDGE,"E45.filletArc"),sQuery(id+"F0.wireOp",EDGE,"E46.filletArc"),sQuery(id+"F0.wireOp",EDGE,"E47.filletArc"),sQuery(id+"F0.wireOp",EDGE,"E48.filletArc"),sQuery(id+"F0.wireOp",EDGE,"E49.filletArc"),sQuery(id+"F0.wireOp",EDGE,"E50.filletArc"),sQuery(id+"F0.wireOp",EDGE,"E51.filletArc"),sQuery(id+"F0.wireOp",EDGE,"E52"),sQuery(id+"F0.wireOp",EDGE,"E53"),sQuery(id+"F0.wireOp",EDGE,"E54"),sQuery(id+"F0.wireOp",EDGE,"E55"),sQuery(id+"F0.wireOp",EDGE,"E56"),sQuery(id+"F0.wireOp",EDGE,"E58"),sQuery(id+"F0.wireOp",EDGE,"E59"),sQuery(id+"F0.wireOp",EDGE,"E60.filletArc"),sQuery(id+"F0.wireOp",EDGE,"E61.filletArc"),sQuery(id+"F0.wireOp",EDGE,"E62.trimOffspring"),sQuery(id+"F0.wireOp",EDGE,"E63.filletArc"),sQuery(id+"F0.wireOp",EDGE,"E64.filletArc"),sQuery(id+"F0.wireOp",EDGE,"E65.filletArc"),sQuery(id+"F0.wireOp",EDGE,"E66.trimOffspring"),sQuery(id+"F0.wireOp",EDGE,"E67.filletArc"),sQuery(id+"F0.wireOp",EDGE,"E68.filletArc"),sQuery(id+"F0.wireOp",EDGE,"E69.filletArc"),sQuery(id+"F0.wireOp",EDGE,"E70"),sQuery(id+"F0.wireOp",EDGE,"E71"),sQuery(id+"F0.wireOp",EDGE,"E72"),sQuery(id+"F0.wireOp",EDGE,"E73"),sQuery(id+"F0.wireOp",EDGE,"E74"),sQuery(id+"F0.wireOp",EDGE,"E75"),sQuery(id+"F0.wireOp",EDGE,"E76"),sQuery(id+"F0.wireOp",EDGE,"E77"),sQuery(id+"F0.wireOp",EDGE,"E78"),sQuery(id+"F0.wireOp",EDGE,"E79"),sQuery(id+"F0.wireOp",EDGE,"E80"),sQuery(id+"F0.wireOp",EDGE,"E81"),sQuery(id+"F0.wireOp",EDGE,"E82.filletArc"),sQuery(id+"F0.wireOp",EDGE,"E83.filletArc"),sQuery(id+"F0.wireOp",EDGE,"E84.filletArc"),sQuery(id+"F0.wireOp",EDGE,"E85.filletArc"),sQuery(id+"F0.wireOp",EDGE,"E86.filletArc"),sQuery(id+"F0.wireOp",EDGE,"E87.filletArc"),sQuery(id+"F0.wireOp",EDGE,"E88.filletArc"),sQuery(id+"F0.wireOp",EDGE,"E89.filletArc"),sQuery(id+"F0.wireOp",EDGE,"E90"),sQuery(id+"F0.wireOp",EDGE,"E91"),sQuery(id+"F0.wireOp",EDGE,"E92"),sQuery(id+"F0.wireOp",EDGE,"E93"),sQuery(id+"F0.wireOp",EDGE,"E94"),sQuery(id+"F0.wireOp",EDGE,"E95"),sQuery(id+"F0.wireOp",EDGE,"E96"),sQuery(id+"F0.wireOp",EDGE,"E97.filletArc"),sQuery(id+"F0.wireOp",EDGE,"E98.filletArc"),sQuery(id+"F0.wireOp",EDGE,"E99.trimOffspring"),sQuery(id+"F0.wireOp",EDGE,"E100.filletArc"),sQuery(id+"F0.wireOp",EDGE,"E101.filletArc"),sQuery(id+"F0.wireOp",EDGE,"E102.filletArc"),sQuery(id+"F0.wireOp",EDGE,"E103.trimOffspring"),sQuery(id+"F0.wireOp",EDGE,"E104.filletArc"),sQuery(id+"F0.wireOp",EDGE,"E105.filletArc"),sQuery(id+"F0.wireOp",EDGE,"E106.filletArc"),sQuery(id+"F0.wireOp",EDGE,"E110"),sQuery(id+"F0.wireOp",EDGE,"E112"),sQuery(id+"F0.wireOp",EDGE,"E118"),sQuery(id+"F0.wireOp",EDGE,"E119"),sQuery(id+"F0.wireOp",EDGE,"E121"),sQuery(id+"F0.wireOp",EDGE,"E122"),sQuery(id+"F0.wireOp",EDGE,"E123"),sQuery(id+"F0.wireOp",EDGE,"E124")])]});
            var Q1;
            Q1=makeQuery(id+"F11.boolean.opBoolean","COPY",FACE,{"derivedFrom":makeQuery(id+"F11.opExtrude","CAP_FACE",FACE,{"disambiguationData":[OSD([sQuery(id+"F0.wireOp",EDGE,"E0"),sQuery(id+"F0.wireOp",EDGE,"E1"),sQuery(id+"F0.wireOp",EDGE,"E2"),sQuery(id+"F0.wireOp",EDGE,"E3"),sQuery(id+"F0.wireOp",EDGE,"E4"),sQuery(id+"F0.wireOp",EDGE,"E5"),sQuery(id+"F0.wireOp",EDGE,"E6"),sQuery(id+"F0.wireOp",EDGE,"E8"),sQuery(id+"F0.wireOp",EDGE,"E9"),sQuery(id+"F0.wireOp",EDGE,"E10"),sQuery(id+"F0.wireOp",EDGE,"E11"),sQuery(id+"F0.wireOp",EDGE,"E17"),sQuery(id+"F0.wireOp",EDGE,"E18"),sQuery(id+"F0.wireOp",EDGE,"E20"),sQuery(id+"F0.wireOp",EDGE,"E21"),sQuery(id+"F0.wireOp",EDGE,"E23"),sQuery(id+"F0.wireOp",EDGE,"E24"),sQuery(id+"F0.wireOp",EDGE,"E26"),sQuery(id+"F0.wireOp",EDGE,"E27"),sQuery(id+"F0.wireOp",EDGE,"E29"),sQuery(id+"F0.wireOp",EDGE,"E30"),sQuery(id+"F0.wireOp",EDGE,"E32"),sQuery(id+"F0.wireOp",EDGE,"E33"),sQuery(id+"F0.wireOp",EDGE,"E34"),sQuery(id+"F0.wireOp",EDGE,"E35"),sQuery(id+"F0.wireOp",EDGE,"E36"),sQuery(id+"F0.wireOp",EDGE,"E37"),sQuery(id+"F0.wireOp",EDGE,"E38"),sQuery(id+"F0.wireOp",EDGE,"E39"),sQuery(id+"F0.wireOp",EDGE,"E40"),sQuery(id+"F0.wireOp",EDGE,"E41"),sQuery(id+"F0.wireOp",EDGE,"E42"),sQuery(id+"F0.wireOp",EDGE,"E43"),sQuery(id+"F0.wireOp",EDGE,"E44.filletArc"),sQuery(id+"F0.wireOp",EDGE,"E45.filletArc"),sQuery(id+"F0.wireOp",EDGE,"E46.filletArc"),sQuery(id+"F0.wireOp",EDGE,"E47.filletArc"),sQuery(id+"F0.wireOp",EDGE,"E48.filletArc"),sQuery(id+"F0.wireOp",EDGE,"E49.filletArc"),sQuery(id+"F0.wireOp",EDGE,"E50.filletArc"),sQuery(id+"F0.wireOp",EDGE,"E51.filletArc"),sQuery(id+"F0.wireOp",EDGE,"E52"),sQuery(id+"F0.wireOp",EDGE,"E53"),sQuery(id+"F0.wireOp",EDGE,"E54"),sQuery(id+"F0.wireOp",EDGE,"E55"),sQuery(id+"F0.wireOp",EDGE,"E56"),sQuery(id+"F0.wireOp",EDGE,"E58"),sQuery(id+"F0.wireOp",EDGE,"E59"),sQuery(id+"F0.wireOp",EDGE,"E60.filletArc"),sQuery(id+"F0.wireOp",EDGE,"E61.filletArc"),sQuery(id+"F0.wireOp",EDGE,"E62.trimOffspring"),sQuery(id+"F0.wireOp",EDGE,"E63.filletArc"),sQuery(id+"F0.wireOp",EDGE,"E64.filletArc"),sQuery(id+"F0.wireOp",EDGE,"E65.filletArc"),sQuery(id+"F0.wireOp",EDGE,"E66.trimOffspring"),sQuery(id+"F0.wireOp",EDGE,"E67.filletArc"),sQuery(id+"F0.wireOp",EDGE,"E68.filletArc"),sQuery(id+"F0.wireOp",EDGE,"E69.filletArc"),sQuery(id+"F0.wireOp",EDGE,"E70"),sQuery(id+"F0.wireOp",EDGE,"E71"),sQuery(id+"F0.wireOp",EDGE,"E72"),sQuery(id+"F0.wireOp",EDGE,"E73"),sQuery(id+"F0.wireOp",EDGE,"E74"),sQuery(id+"F0.wireOp",EDGE,"E75"),sQuery(id+"F0.wireOp",EDGE,"E76"),sQuery(id+"F0.wireOp",EDGE,"E77"),sQuery(id+"F0.wireOp",EDGE,"E78"),sQuery(id+"F0.wireOp",EDGE,"E79"),sQuery(id+"F0.wireOp",EDGE,"E80"),sQuery(id+"F0.wireOp",EDGE,"E81"),sQuery(id+"F0.wireOp",EDGE,"E82.filletArc"),sQuery(id+"F0.wireOp",EDGE,"E83.filletArc"),sQuery(id+"F0.wireOp",EDGE,"E84.filletArc"),sQuery(id+"F0.wireOp",EDGE,"E85.filletArc"),sQuery(id+"F0.wireOp",EDGE,"E86.filletArc"),sQuery(id+"F0.wireOp",EDGE,"E87.filletArc"),sQuery(id+"F0.wireOp",EDGE,"E88.filletArc"),sQuery(id+"F0.wireOp",EDGE,"E89.filletArc"),sQuery(id+"F0.wireOp",EDGE,"E90"),sQuery(id+"F0.wireOp",EDGE,"E91"),sQuery(id+"F0.wireOp",EDGE,"E92"),sQuery(id+"F0.wireOp",EDGE,"E93"),sQuery(id+"F0.wireOp",EDGE,"E94"),sQuery(id+"F0.wireOp",EDGE,"E95"),sQuery(id+"F0.wireOp",EDGE,"E96"),sQuery(id+"F0.wireOp",EDGE,"E97.filletArc"),sQuery(id+"F0.wireOp",EDGE,"E98.filletArc"),sQuery(id+"F0.wireOp",EDGE,"E99.trimOffspring"),sQuery(id+"F0.wireOp",EDGE,"E100.filletArc"),sQuery(id+"F0.wireOp",EDGE,"E101.filletArc"),sQuery(id+"F0.wireOp",EDGE,"E102.filletArc"),sQuery(id+"F0.wireOp",EDGE,"E103.trimOffspring"),sQuery(id+"F0.wireOp",EDGE,"E104.filletArc"),sQuery(id+"F0.wireOp",EDGE,"E105.filletArc"),sQuery(id+"F0.wireOp",EDGE,"E106.filletArc"),sQuery(id+"F0.wireOp",EDGE,"E110"),sQuery(id+"F0.wireOp",EDGE,"E111"),sQuery(id+"F0.wireOp",EDGE,"E112"),sQuery(id+"F0.wireOp",EDGE,"E113"),sQuery(id+"F0.wireOp",EDGE,"E118"),sQuery(id+"F0.wireOp",EDGE,"E119"),sQuery(id+"F0.wireOp",EDGE,"E121"),sQuery(id+"F0.wireOp",EDGE,"E122"),sQuery(id+"F0.wireOp",EDGE,"E123"),sQuery(id+"F0.wireOp",EDGE,"E124")])],"isStart":false})});
            mirror(context, id + "F12", {"operationType" : NewBodyOperationType.ADD, "entities" : qUnion([Q0]), "mirrorPlane" : qUnion([Q1])});
        }
    });
